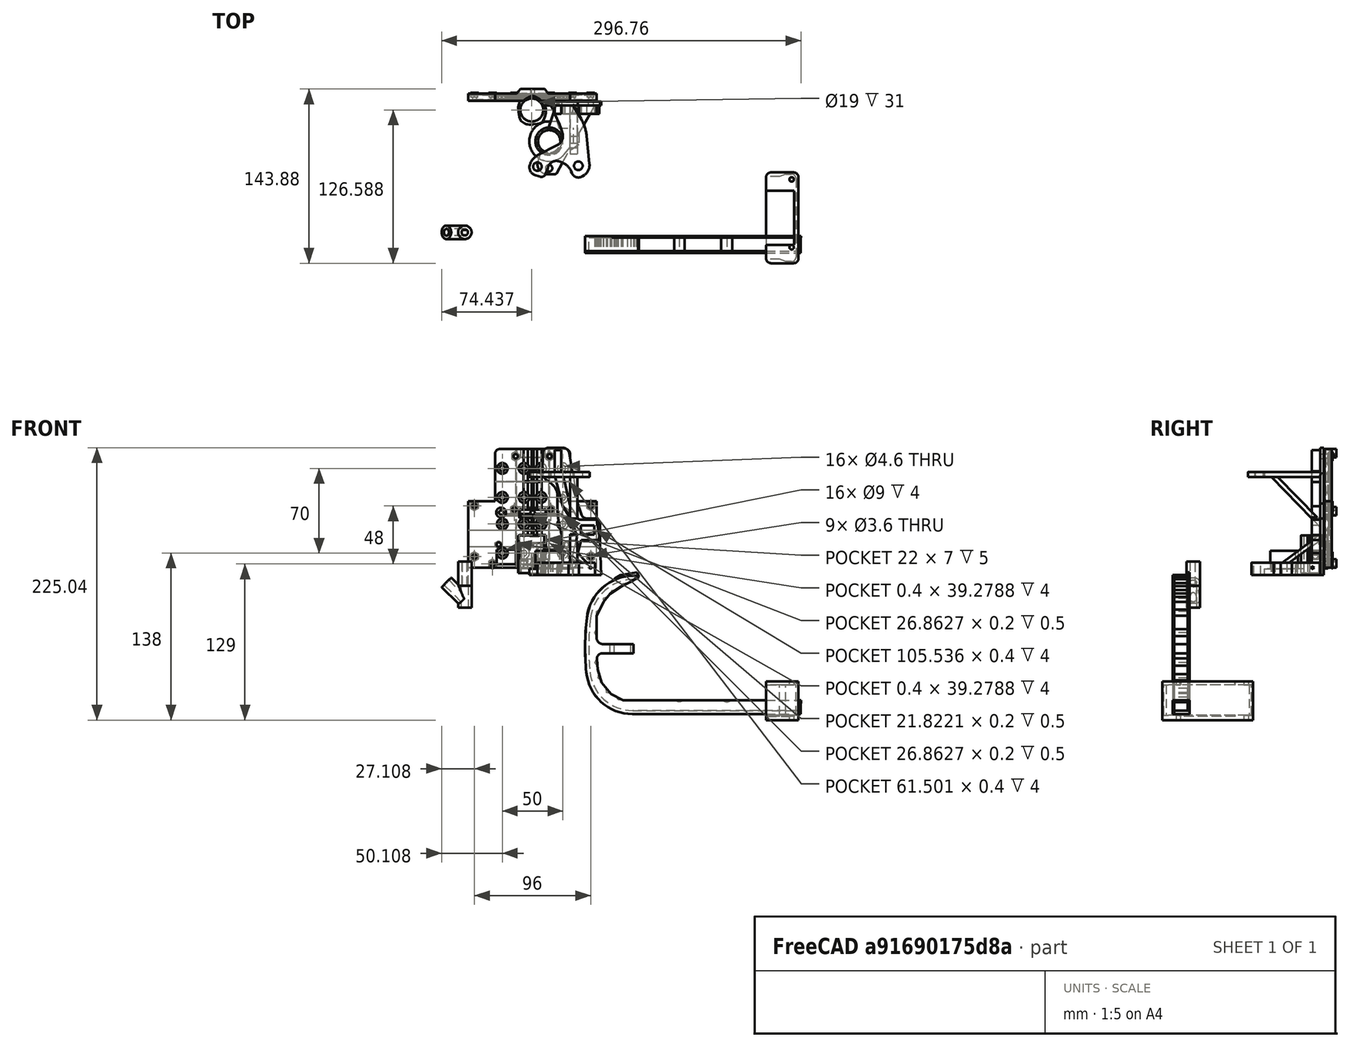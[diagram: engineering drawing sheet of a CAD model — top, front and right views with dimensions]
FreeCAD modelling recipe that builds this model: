
FCSTD DOCUMENT  (FreeCAD 0.18.4R)
Label: pick-and-place
License: All rights reserved
LicenseURL: http://en.wikipedia.org/wiki/All_rights_reserved
objects: Sketcher::SketchObject×44, PartDesign::Pad×22, PartDesign::Pocket×22, PartDesign::Body×8, PartDesign::LinearPattern×1, Mesh::Feature×1
note: 141 computed .brp shape members not serialized (recipe doc carries the construction recipe); baked Part::Feature solids carry a one-line shape summary decoded from their .brp

FEATURE [Sketcher::SketchObject] Sketch110
  AttachmentOffset = pos=(0,0,47) rot=(0,0,1;0rad)
  MapMode = 5
  Placement = pos=(0,-47,-1e-14) rot=(1,0,0;1.5708rad)
  sketch-geometry (4):
    g0: LineSegment StartX=-53 StartY=0 StartZ=0 EndX=53 EndY=0 EndZ=0
    g1: LineSegment StartX=53 StartY=0 StartZ=0 EndX=53 EndY=6 EndZ=0
    g2: LineSegment StartX=53 StartY=6 StartZ=0 EndX=-53 EndY=6 EndZ=0
    g3: LineSegment StartX=-53 StartY=6 StartZ=0 EndX=-53 EndY=0 EndZ=0
  constraints (11):
    c: Coincident(g0,g1)
    c: Coincident(g1,g2)
    c: Coincident(g2,g3)
    c: Coincident(g3,g0)
    c: Horizontal(g0)
    c: Vertical(g1)
    c: Vertical(g3)
    c: PointOnObject(g0,g-1)
    c: Symmetric(g2,g1,g-2)
    c: DistanceY(g1,g1) = 6
    c: DistanceX(g2,g2) = 106
FEATURE [Sketcher::SketchObject] Sketch020
  AttachmentOffset = pos=(-44,0,0) rot=(0,0,1;0rad)
  MapMode = 5
  Placement = pos=(-44,0,0) rot=(0,0,1;0rad)
  sketch-geometry (3):
    g0: Circle CenterX=18 CenterY=-1.5 CenterZ=0 NormalX=0 NormalY=0 NormalZ=1 AngleXU=0 Radius=1.75
    g1: Circle CenterX=44 CenterY=-1.5 CenterZ=0 NormalX=0 NormalY=0 NormalZ=1 AngleXU=0 Radius=1.75
    g2: Circle CenterX=70 CenterY=-1.5 CenterZ=0 NormalX=0 NormalY=0 NormalZ=1 AngleXU=0 Radius=1.75
  constraints (9):
    c: Equal(g1,g2)
    c: Diameter(g2) = 3.5
    c: DistanceX(g-1,g0) = 18
    c: DistanceX(g-1,g1) = 44
    c: DistanceX(g-1,g2) = 70
    c: DistanceY(g0,g-1) = 1.5
    c: Equal(g1,g0)
    c: DistanceY(g1,g0) = 0
    c: DistanceY(g2,g1) = 0
FEATURE [Sketcher::SketchObject] Sketch021
  AttachmentOffset = pos=(0,0,2) rot=(0,0,1;0rad)
  ExternalGeometry = -> [Sketch020]
  MapMode = 5
  Placement = pos=(0,0,2) rot=(0,0,1;0rad)
  sketch-geometry (3):
    g0: Circle CenterX=-26 CenterY=-1.5 CenterZ=0 NormalX=0 NormalY=0 NormalZ=1 AngleXU=0 Radius=3.1
    g1: Circle CenterX=0 CenterY=-1.5 CenterZ=0 NormalX=0 NormalY=0 NormalZ=1 AngleXU=0 Radius=3.1
    g2: Circle CenterX=26 CenterY=-1.5 CenterZ=0 NormalX=0 NormalY=0 NormalZ=1 AngleXU=0 Radius=3.1
  constraints (6):
    c: Coincident(g0,g-3)
    c: Coincident(g1,g-4)
    c: Coincident(g2,g-5)
    c: Equal(g0,g1)
    c: Equal(g1,g2)
    c: Diameter(g2) = 6.2
FEATURE [Sketcher::SketchObject] Sketch290  label="mount-holes"
  MapMode = 5
  sketch-geometry (23):
    g0: Circle CenterX=-25 CenterY=35 CenterZ=0 NormalX=0 NormalY=0 NormalZ=1 AngleXU=0 Radius=2.3
    g1: Circle CenterX=-7 CenterY=35 CenterZ=0 NormalX=0 NormalY=0 NormalZ=1 AngleXU=0 Radius=2.3
    g2: Circle CenterX=-25 CenterY=11 CenterZ=0 NormalX=0 NormalY=0 NormalZ=1 AngleXU=0 Radius=2.3
    g3: Circle CenterX=-7 CenterY=11 CenterZ=0 NormalX=0 NormalY=0 NormalZ=1 AngleXU=0 Radius=2.3
    g4: LineSegment [constr] StartX=-16 StartY=23 StartZ=0 EndX=16 EndY=23 EndZ=0
    g5: LineSegment [constr] StartX=-16 StartY=44 StartZ=0 EndX=-16 EndY=2 EndZ=0
    g6: LineSegment [constr] StartX=16 StartY=44 StartZ=0 EndX=16 EndY=2 EndZ=0
    g7: Circle CenterX=7 CenterY=35 CenterZ=0 NormalX=0 NormalY=0 NormalZ=1 AngleXU=0 Radius=2.3
    g8: Circle CenterX=25 CenterY=35 CenterZ=0 NormalX=0 NormalY=0 NormalZ=1 AngleXU=0 Radius=2.3
    g9: Circle CenterX=7 CenterY=11 CenterZ=0 NormalX=0 NormalY=0 NormalZ=1 AngleXU=0 Radius=2.3
    g10: Circle CenterX=25 CenterY=11 CenterZ=0 NormalX=0 NormalY=0 NormalZ=1 AngleXU=0 Radius=2.3
    g11: LineSegment [constr] StartX=-16 StartY=-23 StartZ=0 EndX=16 EndY=-23 EndZ=0
    g12: LineSegment [constr] StartX=1.74e-14 StartY=-2 StartZ=0 EndX=3.88e-14 EndY=-44 EndZ=0
    g13: Circle CenterX=-25 CenterY=-11 CenterZ=0 NormalX=0 NormalY=0 NormalZ=1 AngleXU=0 Radius=2.3
    g14: Circle CenterX=-7 CenterY=-11 CenterZ=0 NormalX=0 NormalY=0 NormalZ=1 AngleXU=0 Radius=2.3
    g15: Circle CenterX=-25 CenterY=-35 CenterZ=0 NormalX=0 NormalY=0 NormalZ=1 AngleXU=0 Radius=2.3
    g16: Circle CenterX=-7 CenterY=-35 CenterZ=0 NormalX=0 NormalY=0 NormalZ=1 AngleXU=0 Radius=2.3
    g17: LineSegment [constr] StartX=-16 StartY=-3.19826 StartZ=0 EndX=-16 EndY=-38.1346 EndZ=0
    g18: LineSegment [constr] StartX=16 StartY=-4.27965 StartZ=0 EndX=16 EndY=-37.7037 EndZ=0
    g19: Circle CenterX=7 CenterY=-11 CenterZ=0 NormalX=0 NormalY=0 NormalZ=1 AngleXU=0 Radius=2.3
    g20: Circle CenterX=25 CenterY=-11 CenterZ=0 NormalX=0 NormalY=0 NormalZ=1 AngleXU=0 Radius=2.3
    g21: Circle CenterX=7 CenterY=-35 CenterZ=0 NormalX=0 NormalY=0 NormalZ=1 AngleXU=0 Radius=2.3
    g22: Circle CenterX=25 CenterY=-35 CenterZ=0 NormalX=0 NormalY=0 NormalZ=1 AngleXU=0 Radius=2.3
  constraints (47):
    c: Symmetric(g0,g1,g5)
    c: Symmetric(g2,g3,g5)
    c: Symmetric(g0,g2,g4)
    c: DistanceX(g0,g1) = 18
    c: DistanceY(g3,g1) = 24
    c: Equal(g0,g1)
    c: Equal(g0,g2)
    c: Equal(g0,g3)
    c: Diameter(g0) = 4.6
    c: Equal(g1, g7-g10) x4
    c: Symmetric(g7,g9,g4)
    c: Symmetric(g7,g8,g6)
    c: Symmetric(g9,g10,g6)
    c: DistanceX(g7,g8) = 18
    c: Symmetric(g13,g15,g11)
    c: Equal(g2, g13-g16) x4
    c: Symmetric(g3,g9,g12)
    c: DistanceY(g11,g4) = 46
    c: Symmetric(g5,g5,g4)
    c: Symmetric(g6,g6,g4)
    c: Symmetric(g12,g12,g11)
    c: DistanceY(g5,g5) = 42
    c: DistanceY(g6,g6) = 42
    c: DistanceY(g12,g12) = 42
    c: Symmetric(g4,g4,g12)
    c: PointOnObject(g11,g5)
    c: PointOnObject(g11,g6)
    c: Symmetric(g4,g11,g-1)
    c: Symmetric(g1,g7,g-2)
    c: DistanceX(g13,g14) = 18
    c: DistanceY(g15,g13) = 24
    c: Symmetric(g13,g14,g17)
    c: Symmetric(g14,g16,g11)
    c: Symmetric(g15,g16,g17)
    c: DistanceX(g1,g7) = 14
    c: PointOnObject(g17,g5)
    c: Vertical(g18)
    c: PointOnObject(g18,g6)
    c: Equal(g9,g19)
    c: Equal(g19,g20)
    c: Equal(g20,g22)
    c: Equal(g22,g21)
    c: Symmetric(g19,g21,g11)
    c: Symmetric(g20,g22,g11)
    c: Symmetric(g19,g20,g18)
    c: DistanceX(g9,g19) = 0
    c: DistanceY(g19,g14) = 0
FEATURE [Sketcher::SketchObject] Sketch007
  AttachmentOffset = pos=(0,0,2) rot=(0,0,1;0rad)
  ExternalGeometry = -> [Sketch290,Sketch020]
  MapMode = 5
  Placement = pos=(0,0,2) rot=(0,0,1;0rad)
  sketch-geometry (19):
    g0: Circle CenterX=-25 CenterY=35 CenterZ=0 NormalX=0 NormalY=0 NormalZ=1 AngleXU=0 Radius=4.5
    g1: Circle CenterX=-7 CenterY=35 CenterZ=0 NormalX=0 NormalY=0 NormalZ=1 AngleXU=0 Radius=4.5
    g2: Circle CenterX=7 CenterY=35 CenterZ=0 NormalX=0 NormalY=0 NormalZ=1 AngleXU=0 Radius=4.5
    g3: Circle CenterX=25 CenterY=35 CenterZ=0 NormalX=0 NormalY=0 NormalZ=1 AngleXU=0 Radius=4.5
    g4: Circle CenterX=-25 CenterY=11 CenterZ=0 NormalX=0 NormalY=0 NormalZ=1 AngleXU=0 Radius=4.5
    g5: Circle CenterX=-7 CenterY=11 CenterZ=0 NormalX=0 NormalY=0 NormalZ=1 AngleXU=0 Radius=4.5
    g6: Circle CenterX=7 CenterY=11 CenterZ=0 NormalX=0 NormalY=0 NormalZ=1 AngleXU=0 Radius=4.5
    g7: Circle CenterX=25 CenterY=11 CenterZ=0 NormalX=0 NormalY=0 NormalZ=1 AngleXU=0 Radius=4.5
    g8: Circle CenterX=-25 CenterY=-11 CenterZ=0 NormalX=0 NormalY=0 NormalZ=1 AngleXU=0 Radius=4.5
    g9: Circle CenterX=-7 CenterY=-11 CenterZ=0 NormalX=0 NormalY=0 NormalZ=1 AngleXU=0 Radius=4.5
    g10: Circle CenterX=-25 CenterY=-35 CenterZ=0 NormalX=0 NormalY=0 NormalZ=1 AngleXU=0 Radius=4.5
    g11: Circle CenterX=-7 CenterY=-35 CenterZ=0 NormalX=0 NormalY=0 NormalZ=1 AngleXU=0 Radius=4.5
    g12: Circle CenterX=-26 CenterY=-1.5 CenterZ=0 NormalX=0 NormalY=0 NormalZ=1 AngleXU=0 Radius=4.1
    g13: Circle CenterX=0 CenterY=-1.5 CenterZ=0 NormalX=0 NormalY=0 NormalZ=1 AngleXU=0 Radius=4.1
    g14: Circle CenterX=26 CenterY=-1.5 CenterZ=0 NormalX=0 NormalY=0 NormalZ=1 AngleXU=0 Radius=4.1
    g15: Circle CenterX=7 CenterY=-11 CenterZ=0 NormalX=0 NormalY=0 NormalZ=1 AngleXU=0 Radius=4.5
    g16: Circle CenterX=25 CenterY=-11 CenterZ=0 NormalX=0 NormalY=0 NormalZ=1 AngleXU=0 Radius=4.5
    g17: Circle CenterX=7 CenterY=-35 CenterZ=0 NormalX=0 NormalY=0 NormalZ=1 AngleXU=0 Radius=4.5
    g18: Circle CenterX=25 CenterY=-35 CenterZ=0 NormalX=0 NormalY=0 NormalZ=1 AngleXU=0 Radius=4.5
FEATURE [Sketcher::SketchObject] Sketch001
  ExternalGeometry = -> [Sketch290]
  MapMode = 5
  sketch-geometry (8):
    g0: LineSegment StartX=-27 StartY=51 StartZ=0 EndX=27 EndY=51 EndZ=0
    g1: LineSegment StartX=31 StartY=47 StartZ=0 EndX=31 EndY=-43 EndZ=0
    g2: LineSegment StartX=27 StartY=-47 StartZ=0 EndX=-27 EndY=-47 EndZ=0
    g3: ArcOfCircle CenterX=-27 CenterY=47 CenterZ=0 NormalX=0 NormalY=0 NormalZ=1 AngleXU=0 Radius=4 StartAngle=1.5708 EndAngle=3.14159
    g4: ArcOfCircle CenterX=27 CenterY=47 CenterZ=0 NormalX=0 NormalY=0 NormalZ=1 AngleXU=0 Radius=4 StartAngle=6e-16 EndAngle=1.5708
    g5: ArcOfCircle CenterX=-27 CenterY=-43 CenterZ=0 NormalX=0 NormalY=0 NormalZ=1 AngleXU=0 Radius=4 StartAngle=3.14114 EndAngle=4.71239
    g6: ArcOfCircle CenterX=27 CenterY=-43 CenterZ=0 NormalX=0 NormalY=0 NormalZ=1 AngleXU=0 Radius=4 StartAngle=4.71239 EndAngle=6.28319
    g7: LineSegment StartX=-31 StartY=-42.9982 StartZ=0 EndX=-31 EndY=47 EndZ=0
  constraints (20):
    c: Horizontal(g2)
    c: Vertical(g1)
    c: Tangent(g0,g3) = 1.5708
    c: Tangent(g0,g4) = 1.5708
    c: Tangent(g1,g4) = 1.5708
    c: Tangent(g2,g5) = 1.5708
    c: Tangent(g2,g6) = 1.5708
    c: Tangent(g1,g6) = 1.5708
    c: Radius(g3) = 4
    c: Equal(g3,g4)
    c: Equal(g4,g6)
    c: Equal(g6,g5)
    c: Symmetric(g0,g0,g-2)
    c: DistanceY(g2,g-5) = 12
    c: DistanceY(g-3,g0) = 16
    c: Coincident(g7,g5)
    c: Vertical(g7)
    c: DistanceX(g3,g-3) = 6
    c: Coincident(g7,g3)
    c: Tangent(g3,g7)
FEATURE [PartDesign::Pad] Pad060
  Length = 6
  Length2 = 100
  Profile = -> Sketch001
  Type = 0
FEATURE [PartDesign::Pad] Pad016
  BaseFeature = -> Pad060
  Length = 55
  Length2 = 100
  Profile = -> Sketch110
  Reversed = true
  Type = 0
FEATURE [Sketcher::SketchObject] Sketch294
  MapMode = 5
  sketch-geometry (10):
    g0: Circle CenterX=-15 CenterY=1 CenterZ=0 NormalX=0 NormalY=0 NormalZ=1 AngleXU=0 Radius=1.8
    g1: Circle CenterX=-33 CenterY=-44 CenterZ=0 NormalX=0 NormalY=0 NormalZ=1 AngleXU=0 Radius=1.8
    g2: Circle CenterX=-48 CenterY=4 CenterZ=0 NormalX=0 NormalY=0 NormalZ=1 AngleXU=0 Radius=1.8
    g3: Circle CenterX=-48 CenterY=-38 CenterZ=0 NormalX=0 NormalY=0 NormalZ=1 AngleXU=0 Radius=1.8
    g4: Circle CenterX=15 CenterY=1 CenterZ=0 NormalX=0 NormalY=0 NormalZ=1 AngleXU=0 Radius=1.8
    g5: Circle CenterX=33 CenterY=-44 CenterZ=0 NormalX=0 NormalY=0 NormalZ=1 AngleXU=0 Radius=1.8
    g6: Circle CenterX=48 CenterY=-38 CenterZ=0 NormalX=0 NormalY=0 NormalZ=1 AngleXU=0 Radius=1.8
    g7: Circle CenterX=48 CenterY=4 CenterZ=0 NormalX=0 NormalY=0 NormalZ=1 AngleXU=0 Radius=1.8
    g8: Circle CenterX=-14 CenterY=45 CenterZ=0 NormalX=0 NormalY=0 NormalZ=1 AngleXU=0 Radius=1.8
    g9: Circle CenterX=14 CenterY=45 CenterZ=0 NormalX=0 NormalY=0 NormalZ=1 AngleXU=0 Radius=1.8
  constraints (25):
    c: Diameter(g1) = 3.6
    c: DistanceX(g1) = -33
    c: DistanceY(g1) = -44
    c: Equal(g1,g0)
    c: Equal(g0,g2)
    c: Equal(g2,g3)
    c: DistanceX(g3) = -48
    c: DistanceX(g2) = -48
    c: DistanceX(g0) = -15
    c: DistanceY(g0) = 1
    c: Equal(g0,g4)
    c: Equal(g4,g7)
    c: Equal(g7,g6)
    c: Equal(g6,g5)
    c: Symmetric(g1,g5,g-2)
    c: Symmetric(g6,g3,g-2)
    c: Symmetric(g2,g7,g-2)
    c: Symmetric(g0,g4,g-2)
    c: DistanceY(g-1,g2) = 4
    c: Equal(g8,g4)
    c: DistanceX(g8) = -14
    c: DistanceY(g8) = 45
    c: Symmetric(g8,g9,g-2)
    c: Equal(g8,g9)
    c: DistanceY(g3,g1) = -6
FEATURE [Sketcher::SketchObject] Sketch295
  AttachmentOffset = pos=(0,0,3) rot=(0,0,1;0rad)
  ExternalGeometry = -> [Sketch294]
  MapMode = 5
  Placement = pos=(0,0,3) rot=(0,0,1;0rad)
  sketch-geometry (70):
    g0: LineSegment StartX=-45.2 StartY=-36.3834 StartZ=0 EndX=-48 EndY=-34.7668 EndZ=0
    g1: LineSegment StartX=-48 StartY=-34.7668 StartZ=0 EndX=-50.8 EndY=-36.3834 EndZ=0
    g2: LineSegment StartX=-50.8 StartY=-36.3834 StartZ=0 EndX=-50.8 EndY=-39.6166 EndZ=0
    g3: LineSegment StartX=-50.8 StartY=-39.6166 StartZ=0 EndX=-48 EndY=-41.2332 EndZ=0
    g4: LineSegment StartX=-48 StartY=-41.2332 StartZ=0 EndX=-45.2 EndY=-39.6166 EndZ=0
    g5: LineSegment StartX=-45.2 StartY=-39.6166 StartZ=0 EndX=-45.2 EndY=-36.3834 EndZ=0
    g6: Circle [constr] CenterX=-48 CenterY=-38 CenterZ=0 NormalX=0 NormalY=0 NormalZ=1 AngleXU=0 Radius=3.23316
    g7: LineSegment StartX=-30.2 StartY=-42.3834 StartZ=0 EndX=-33 EndY=-40.7668 EndZ=0
    g8: LineSegment StartX=-33 StartY=-40.7668 StartZ=0 EndX=-35.8 EndY=-42.3834 EndZ=0
    g9: LineSegment StartX=-35.8 StartY=-42.3834 StartZ=0 EndX=-35.8 EndY=-45.6166 EndZ=0
    g10: LineSegment StartX=-35.8 StartY=-45.6166 StartZ=0 EndX=-33 EndY=-47.2332 EndZ=0
    g11: LineSegment StartX=-33 StartY=-47.2332 StartZ=0 EndX=-30.2 EndY=-45.6166 EndZ=0
    g12: LineSegment StartX=-30.2 StartY=-45.6166 StartZ=0 EndX=-30.2 EndY=-42.3834 EndZ=0
    g13: Circle [constr] CenterX=-33 CenterY=-44 CenterZ=0 NormalX=0 NormalY=0 NormalZ=1 AngleXU=0 Radius=3.23316
    g14: LineSegment StartX=-45.2 StartY=5.61658 StartZ=0 EndX=-48 EndY=7.23316 EndZ=0
    g15: LineSegment StartX=-48 StartY=7.23316 StartZ=0 EndX=-50.8 EndY=5.61658 EndZ=0
    g16: LineSegment StartX=-50.8 StartY=5.61658 StartZ=0 EndX=-50.8 EndY=2.38342 EndZ=0
    g17: LineSegment StartX=-50.8 StartY=2.38342 StartZ=0 EndX=-48 EndY=0.766838 EndZ=0
    g18: LineSegment StartX=-48 StartY=0.766838 StartZ=0 EndX=-45.2 EndY=2.38342 EndZ=0
    g19: LineSegment StartX=-45.2 StartY=2.38342 StartZ=0 EndX=-45.2 EndY=5.61658 EndZ=0
    g20: Circle [constr] CenterX=-48 CenterY=4 CenterZ=0 NormalX=0 NormalY=0 NormalZ=1 AngleXU=0 Radius=3.23316
    g21: LineSegment StartX=-12.2 StartY=2.61658 StartZ=0 EndX=-15 EndY=4.23316 EndZ=0
    g22: LineSegment StartX=-15 StartY=4.23316 StartZ=0 EndX=-17.8 EndY=2.61658 EndZ=0
    g23: LineSegment StartX=-17.8 StartY=2.61658 StartZ=0 EndX=-17.8 EndY=-0.616581 EndZ=0
    g24: LineSegment StartX=-17.8 StartY=-0.616581 StartZ=0 EndX=-15 EndY=-2.23316 EndZ=0
    g25: LineSegment StartX=-15 StartY=-2.23316 StartZ=0 EndX=-12.2 EndY=-0.616581 EndZ=0
    g26: LineSegment StartX=-12.2 StartY=-0.616581 StartZ=0 EndX=-12.2 EndY=2.61658 EndZ=0
    g27: Circle [constr] CenterX=-15 CenterY=1 CenterZ=0 NormalX=0 NormalY=0 NormalZ=1 AngleXU=0 Radius=3.23316
    g28: LineSegment StartX=-11.2 StartY=46.6166 StartZ=0 EndX=-14 EndY=48.2332 EndZ=0
    g29: LineSegment StartX=-14 StartY=48.2332 StartZ=0 EndX=-16.8 EndY=46.6166 EndZ=0
    g30: LineSegment StartX=-16.8 StartY=46.6166 StartZ=0 EndX=-16.8 EndY=43.3834 EndZ=0
    g31: LineSegment StartX=-16.8 StartY=43.3834 StartZ=0 EndX=-14 EndY=41.7668 EndZ=0
    g32: LineSegment StartX=-14 StartY=41.7668 StartZ=0 EndX=-11.2 EndY=43.3834 EndZ=0
    g33: LineSegment StartX=-11.2 StartY=43.3834 StartZ=0 EndX=-11.2 EndY=46.6166 EndZ=0
    g34: Circle [constr] CenterX=-14 CenterY=45 CenterZ=0 NormalX=0 NormalY=0 NormalZ=1 AngleXU=0 Radius=3.23316
    g35: LineSegment StartX=16.8 StartY=46.6166 StartZ=0 EndX=14 EndY=48.2332 EndZ=0
    g36: LineSegment StartX=14 StartY=48.2332 StartZ=0 EndX=11.2 EndY=46.6166 EndZ=0
    g37: LineSegment StartX=11.2 StartY=46.6166 StartZ=0 EndX=11.2 EndY=43.3834 EndZ=0
    g38: LineSegment StartX=11.2 StartY=43.3834 StartZ=0 EndX=14 EndY=41.7668 EndZ=0
    g39: LineSegment StartX=14 StartY=41.7668 StartZ=0 EndX=16.8 EndY=43.3834 EndZ=0
    g40: LineSegment StartX=16.8 StartY=43.3834 StartZ=0 EndX=16.8 EndY=46.6166 EndZ=0
    g41: Circle [constr] CenterX=14 CenterY=45 CenterZ=0 NormalX=0 NormalY=0 NormalZ=1 AngleXU=0 Radius=3.23316
    g42: LineSegment StartX=17.8 StartY=2.61658 StartZ=0 EndX=15 EndY=4.23316 EndZ=0
    g43: LineSegment StartX=15 StartY=4.23316 StartZ=0 EndX=12.2 EndY=2.61658 EndZ=0
    g44: LineSegment StartX=12.2 StartY=2.61658 StartZ=0 EndX=12.2 EndY=-0.616581 EndZ=0
    g45: LineSegment StartX=12.2 StartY=-0.616581 StartZ=0 EndX=15 EndY=-2.23316 EndZ=0
    g46: LineSegment StartX=15 StartY=-2.23316 StartZ=0 EndX=17.8 EndY=-0.616581 EndZ=0
    g47: LineSegment StartX=17.8 StartY=-0.616581 StartZ=0 EndX=17.8 EndY=2.61658 EndZ=0
    g48: Circle [constr] CenterX=15 CenterY=1 CenterZ=0 NormalX=0 NormalY=0 NormalZ=1 AngleXU=0 Radius=3.23316
    g49: LineSegment StartX=50.8 StartY=5.61658 StartZ=0 EndX=48 EndY=7.23316 EndZ=0
    g50: LineSegment StartX=48 StartY=7.23316 StartZ=0 EndX=45.2 EndY=5.61658 EndZ=0
    g51: LineSegment StartX=45.2 StartY=5.61658 StartZ=0 EndX=45.2 EndY=2.38342 EndZ=0
    g52: LineSegment StartX=45.2 StartY=2.38342 StartZ=0 EndX=48 EndY=0.766838 EndZ=0
    g53: LineSegment StartX=48 StartY=0.766838 StartZ=0 EndX=50.8 EndY=2.38342 EndZ=0
    g54: LineSegment StartX=50.8 StartY=2.38342 StartZ=0 EndX=50.8 EndY=5.61658 EndZ=0
    g55: Circle [constr] CenterX=48 CenterY=4 CenterZ=0 NormalX=0 NormalY=0 NormalZ=1 AngleXU=0 Radius=3.23316
    g56: LineSegment StartX=35.8 StartY=-42.3834 StartZ=0 EndX=33 EndY=-40.7668 EndZ=0
    g57: LineSegment StartX=33 StartY=-40.7668 StartZ=0 EndX=30.2 EndY=-42.3834 EndZ=0
    g58: LineSegment StartX=30.2 StartY=-42.3834 StartZ=0 EndX=30.2 EndY=-45.6166 EndZ=0
    g59: LineSegment StartX=30.2 StartY=-45.6166 StartZ=0 EndX=33 EndY=-47.2332 EndZ=0
    g60: LineSegment StartX=33 StartY=-47.2332 StartZ=0 EndX=35.8 EndY=-45.6166 EndZ=0
    g61: LineSegment StartX=35.8 StartY=-45.6166 StartZ=0 EndX=35.8 EndY=-42.3834 EndZ=0
    g62: Circle [constr] CenterX=33 CenterY=-44 CenterZ=0 NormalX=0 NormalY=0 NormalZ=1 AngleXU=0 Radius=3.23316
    g63: LineSegment StartX=50.8 StartY=-36.3834 StartZ=0 EndX=48 EndY=-34.7668 EndZ=0
    g64: LineSegment StartX=48 StartY=-34.7668 StartZ=0 EndX=45.2 EndY=-36.3834 EndZ=0
    g65: LineSegment StartX=45.2 StartY=-36.3834 StartZ=0 EndX=45.2 EndY=-39.6166 EndZ=0
    g66: LineSegment StartX=45.2 StartY=-39.6166 StartZ=0 EndX=48 EndY=-41.2332 EndZ=0
    g67: LineSegment StartX=48 StartY=-41.2332 StartZ=0 EndX=50.8 EndY=-39.6166 EndZ=0
    g68: LineSegment StartX=50.8 StartY=-39.6166 StartZ=0 EndX=50.8 EndY=-36.3834 EndZ=0
    g69: Circle [constr] CenterX=48 CenterY=-38 CenterZ=0 NormalX=0 NormalY=0 NormalZ=1 AngleXU=0 Radius=3.23316
  constraints (160):
    c: Coincident(g0,g1)
    c: Coincident(g1,g2)
    c: Coincident(g2,g3)
    c: Coincident(g3,g4)
    c: Coincident(g4,g5)
    c: Coincident(g5,g0)
    c: Equal(g0, g1-g5) x5
    c: PointOnObject(g0,g6)
    c: PointOnObject(g1,g6)
    c: PointOnObject(g2,g6)
    c: PointOnObject(g3,g6)
    c: PointOnObject(g4,g6)
    c: PointOnObject(g5,g6)
    c: Coincident(g6,g-6)
    c: Coincident(g7,g8)
    c: Coincident(g8,g9)
    c: Coincident(g9,g10)
    c: Coincident(g10,g11)
    c: Coincident(g11,g12)
    c: Coincident(g12,g7)
    c: Equal(g7, g8-g12) x5
    c: PointOnObject(g7,g13)
    c: PointOnObject(g8,g13)
    c: PointOnObject(g9,g13)
    c: PointOnObject(g10,g13)
    c: PointOnObject(g11,g13)
    c: PointOnObject(g12,g13)
    c: Coincident(g13,g-7)
    c: Coincident(g14,g15)
    c: Coincident(g15,g16)
    c: Coincident(g16,g17)
    c: Coincident(g17,g18)
    c: Coincident(g18,g19)
    c: Coincident(g19,g14)
    c: Equal(g14, g15-g19) x5
    c: PointOnObject(g14,g20)
    c: PointOnObject(g15,g20)
    c: PointOnObject(g16,g20)
    c: PointOnObject(g17,g20)
    c: PointOnObject(g18,g20)
    c: PointOnObject(g19,g20)
    c: Coincident(g20,g-3)
    c: Coincident(g21,g22)
    c: Coincident(g22,g23)
    c: Coincident(g23,g24)
    c: Coincident(g24,g25)
    c: Coincident(g25,g26)
    c: Coincident(g26,g21)
    c: Equal(g21, g22-g26) x5
    c: PointOnObject(g21,g27)
    c: PointOnObject(g22,g27)
    c: PointOnObject(g23,g27)
    c: PointOnObject(g24,g27)
    c: PointOnObject(g25,g27)
    c: PointOnObject(g26,g27)
    c: Coincident(g27,g-5)
    c: Coincident(g28,g29)
    c: Coincident(g29,g30)
    c: Coincident(g30,g31)
    c: Coincident(g31,g32)
    c: Coincident(g32,g33)
    c: Coincident(g33,g28)
    c: Equal(g28, g29-g33) x5
    c: PointOnObject(g28,g34)
    c: PointOnObject(g29,g34)
    c: PointOnObject(g30,g34)
    c: PointOnObject(g31,g34)
    c: PointOnObject(g32,g34)
    c: PointOnObject(g33,g34)
    c: Coincident(g34,g-11)
    c: Coincident(g35,g36)
    c: Coincident(g36,g37)
    c: Coincident(g37,g38)
    c: Coincident(g38,g39)
    c: Coincident(g39,g40)
    c: Coincident(g40,g35)
    c: Equal(g35, g36-g40) x5
    c: PointOnObject(g35,g41)
    c: PointOnObject(g36,g41)
    c: PointOnObject(g37,g41)
    c: PointOnObject(g38,g41)
    c: PointOnObject(g39,g41)
    c: PointOnObject(g40,g41)
    c: Coincident(g41,g-12)
    c: Coincident(g42,g43)
    c: Coincident(g43,g44)
    c: Coincident(g44,g45)
    c: Coincident(g45,g46)
    c: Coincident(g46,g47)
    c: Coincident(g47,g42)
    c: Equal(g42, g43-g47) x5
    c: PointOnObject(g42,g48)
    c: PointOnObject(g43,g48)
    c: PointOnObject(g44,g48)
    c: PointOnObject(g45,g48)
    c: PointOnObject(g46,g48)
    c: PointOnObject(g47,g48)
    c: Coincident(g48,g-4)
    c: Coincident(g49,g50)
    c: Coincident(g50,g51)
    c: Coincident(g51,g52)
    c: Coincident(g52,g53)
    c: Coincident(g53,g54)
    c: Coincident(g54,g49)
    c: Equal(g49, g50-g54) x5
    c: PointOnObject(g49,g55)
    c: PointOnObject(g50,g55)
    c: PointOnObject(g51,g55)
    c: PointOnObject(g52,g55)
    c: PointOnObject(g53,g55)
    c: PointOnObject(g54,g55)
    c: Coincident(g55,g-10)
    c: Coincident(g56,g57)
    c: Coincident(g57,g58)
    c: Coincident(g58,g59)
    c: Coincident(g59,g60)
    c: Coincident(g60,g61)
    c: Coincident(g61,g56)
    c: Equal(g56, g57-g61) x5
    c: PointOnObject(g56,g62)
    c: PointOnObject(g57,g62)
    c: PointOnObject(g58,g62)
    c: PointOnObject(g59,g62)
    c: PointOnObject(g60,g62)
    c: PointOnObject(g61,g62)
    c: Coincident(g62,g-8)
    c: Coincident(g63,g64)
    c: Coincident(g64,g65)
    c: Coincident(g65,g66)
    c: Coincident(g66,g67)
    c: Coincident(g67,g68)
    c: Coincident(g68,g63)
    c: Equal(g63, g64-g68) x5
    c: PointOnObject(g63,g69)
    c: PointOnObject(g64,g69)
    c: PointOnObject(g65,g69)
    c: PointOnObject(g66,g69)
    c: PointOnObject(g67,g69)
    c: PointOnObject(g68,g69)
    c: Coincident(g69,g-9)
    c: Vertical(g5)
    c: Vertical(g12)
    c: Vertical(g61)
    c: Vertical(g68)
    c: Vertical(g54)
    c: Vertical(g47)
    c: Vertical(g40)
    c: Vertical(g33)
    c: Vertical(g26)
    c: Vertical(g19)
    c: DistanceX(g29,g28) = 5.6
    c: Equal(g33,g40)
    c: Equal(g40,g19)
    c: Equal(g19,g26)
    c: Equal(g26,g47)
    c: Equal(g47,g54)
    c: Equal(g68,g54)
    c: Equal(g68,g61)
    c: Equal(g61,g12)
    c: Equal(g5,g12)
FEATURE [Sketcher::SketchObject] Sketch299
  AttachmentOffset = pos=(0,0,5) rot=(0,0,1;0rad)
  MapMode = 5
  Placement = pos=(0,0,5) rot=(0,0,1;0rad)
  sketch-geometry (28):
    g0: LineSegment StartX=-30.7505 StartY=24.2507 StartZ=0 EndX=30.7505 EndY=24.2507 EndZ=0
    g1: LineSegment StartX=30.7505 StartY=24.2507 StartZ=0 EndX=30.7505 EndY=23.8507 EndZ=0
    g2: LineSegment StartX=30.7505 StartY=23.8507 StartZ=0 EndX=-30.7505 EndY=23.8507 EndZ=0
    g3: LineSegment StartX=-30.7505 StartY=23.8507 StartZ=0 EndX=-30.7505 EndY=24.2507 EndZ=0
    g4: LineSegment StartX=-52.7681 StartY=-15.8802 StartZ=0 EndX=52.7681 EndY=-15.8802 EndZ=0
    g5: LineSegment StartX=52.7681 StartY=-15.8802 StartZ=0 EndX=52.7681 EndY=-16.2802 EndZ=0
    g6: LineSegment StartX=52.7681 StartY=-16.2802 StartZ=0 EndX=-52.7681 EndY=-16.2802 EndZ=0
    g7: LineSegment StartX=-52.7681 StartY=-16.2802 StartZ=0 EndX=-52.7681 EndY=-15.8802 EndZ=0
    g8: LineSegment StartX=-52.749 StartY=-29.5495 StartZ=0 EndX=52.749 EndY=-29.5495 EndZ=0
    g9: LineSegment StartX=52.749 StartY=-29.5495 StartZ=0 EndX=52.749 EndY=-29.9495 EndZ=0
    g10: LineSegment StartX=52.749 StartY=-29.9495 StartZ=0 EndX=-52.749 EndY=-29.9495 EndZ=0
    g11: LineSegment StartX=-52.749 StartY=-29.9495 StartZ=0 EndX=-52.749 EndY=-29.5495 EndZ=0
    g12: LineSegment StartX=-13.8862 StartY=50.9099 StartZ=0 EndX=-13.4862 EndY=50.9099 EndZ=0
    g13: LineSegment StartX=-13.4862 StartY=50.9099 StartZ=0 EndX=-13.4862 EndY=0.587471 EndZ=0
    g14: LineSegment StartX=-13.4862 StartY=0.587471 StartZ=0 EndX=-13.8862 EndY=0.587471 EndZ=0
    g15: LineSegment StartX=-13.8862 StartY=0.587471 StartZ=0 EndX=-13.8862 EndY=50.9099 EndZ=0
    g16: LineSegment StartX=13.4862 StartY=50.9099 StartZ=0 EndX=13.8862 EndY=50.9099 EndZ=0
    g17: LineSegment StartX=13.8862 StartY=50.9099 StartZ=0 EndX=13.8862 EndY=0.587471 EndZ=0
    g18: LineSegment StartX=13.8862 StartY=0.587471 StartZ=0 EndX=13.4862 EndY=0.587471 EndZ=0
    g19: LineSegment StartX=13.4862 StartY=0.587471 StartZ=0 EndX=13.4862 EndY=50.9099 EndZ=0
    g20: LineSegment StartX=13.4862 StartY=-7.08749 StartZ=0 EndX=13.8862 EndY=-7.08749 EndZ=0
    g21: LineSegment StartX=13.8862 StartY=-7.08749 StartZ=0 EndX=13.8862 EndY=-46.3663 EndZ=0
    g22: LineSegment StartX=13.8862 StartY=-46.3663 StartZ=0 EndX=13.4862 EndY=-46.3663 EndZ=0
    g23: LineSegment StartX=13.4862 StartY=-46.3663 StartZ=0 EndX=13.4862 EndY=-7.08749 EndZ=0
    g24: LineSegment StartX=-13.8862 StartY=-7.08749 StartZ=0 EndX=-13.4862 EndY=-7.08749 EndZ=0
    g25: LineSegment StartX=-13.4862 StartY=-7.08749 StartZ=0 EndX=-13.4862 EndY=-46.3663 EndZ=0
    g26: LineSegment StartX=-13.4862 StartY=-46.3663 StartZ=0 EndX=-13.8862 EndY=-46.3663 EndZ=0
    g27: LineSegment StartX=-13.8862 StartY=-46.3663 StartZ=0 EndX=-13.8862 EndY=-7.08749 EndZ=0
  constraints (66):
    c: Coincident(g0,g1)
    c: Coincident(g1,g2)
    c: Coincident(g2,g3)
    c: Coincident(g3,g0)
    c: Horizontal(g2)
    c: Vertical(g1)
    c: Vertical(g3)
    c: Coincident(g4,g5)
    c: Coincident(g5,g6)
    c: Coincident(g6,g7)
    c: Coincident(g7,g4)
    c: Horizontal(g6)
    c: Vertical(g5)
    c: Vertical(g7)
    c: Coincident(g8,g9)
    c: Coincident(g9,g10)
    c: Coincident(g10,g11)
    c: Coincident(g11,g8)
    c: Horizontal(g10)
    c: Vertical(g9)
    c: Vertical(g11)
    c: Coincident(g12,g13)
    c: Coincident(g13,g14)
    c: Coincident(g14,g15)
    c: Coincident(g15,g12)
    c: Horizontal(g12)
    c: Horizontal(g14)
    c: Vertical(g13)
    c: Vertical(g15)
    c: Coincident(g16,g17)
    c: Coincident(g17,g18)
    c: Coincident(g18,g19)
    c: Coincident(g19,g16)
    c: Horizontal(g16)
    c: Horizontal(g18)
    c: Vertical(g17)
    c: DistanceY(g5,g5) = 0.4
    c: Equal(g5,g9)
    c: Equal(g9,g16)
    c: Equal(g16,g12)
    c: Symmetric(g12,g16,g-2)
    c: Equal(g16,g1)
    c: Symmetric(g0,g0,g-2)
    c: Symmetric(g4,g4,g-2)
    c: Symmetric(g8,g8,g-2)
    c: Symmetric(g13,g18,g-2)
    c: Coincident(g20,g21)
    c: Coincident(g21,g22)
    c: Coincident(g22,g23)
    c: Coincident(g23,g20)
    c: Horizontal(g20)
    c: Horizontal(g22)
    c: Vertical(g21)
    c: Vertical(g23)
    c: Coincident(g24,g25)
    c: Coincident(g25,g26)
    c: Coincident(g26,g27)
    c: Coincident(g27,g24)
    c: Horizontal(g24)
    c: Horizontal(g26)
    c: Vertical(g27)
    c: PointOnObject(g24,g15)
    c: PointOnObject(g24,g13)
    c: PointOnObject(g20,g17)
    c: Symmetric(g24,g20,g-2)
    c: Symmetric(g25,g22,g-2)
FEATURE [Sketcher::SketchObject] Sketch300
  AttachmentOffset = pos=(0,0,0.5) rot=(0,0,1;0rad)
  MapMode = 5
  Placement = pos=(0,0,0.5) rot=(0,0,1;0rad)
  sketch-geometry (16):
    g0: LineSegment StartX=-23.8387 StartY=-2.6808 StartZ=0 EndX=-2.0166 EndY=-2.6808 EndZ=0
    g1: LineSegment StartX=-2.0166 StartY=-2.6808 StartZ=0 EndX=-2.0166 EndY=-2.4808 EndZ=0
    g2: LineSegment StartX=-2.0166 StartY=-2.4808 StartZ=0 EndX=-23.8387 EndY=-2.4808 EndZ=0
    g3: LineSegment StartX=-23.8387 StartY=-2.4808 StartZ=0 EndX=-23.8387 EndY=-2.6808 EndZ=0
    g4: LineSegment StartX=-27.5679 StartY=-4.24296 StartZ=0 EndX=-0.705224 EndY=-4.24296 EndZ=0
    g5: LineSegment StartX=-0.705224 StartY=-4.24296 StartZ=0 EndX=-0.705224 EndY=-4.44296 EndZ=0
    g6: LineSegment StartX=-0.705224 StartY=-4.44296 StartZ=0 EndX=-27.5679 EndY=-4.44296 EndZ=0
    g7: LineSegment StartX=-27.5679 StartY=-4.44296 StartZ=0 EndX=-27.5679 EndY=-4.24296 EndZ=0
    g8: LineSegment StartX=2.0166 StartY=-2.4808 StartZ=0 EndX=23.8387 EndY=-2.4808 EndZ=0
    g9: LineSegment StartX=23.8387 StartY=-2.4808 StartZ=0 EndX=23.8387 EndY=-2.6808 EndZ=0
    g10: LineSegment StartX=23.8387 StartY=-2.6808 StartZ=0 EndX=2.0166 EndY=-2.6808 EndZ=0
    g11: LineSegment StartX=2.0166 StartY=-2.6808 StartZ=0 EndX=2.0166 EndY=-2.4808 EndZ=0
    g12: LineSegment StartX=0.705224 StartY=-4.24296 StartZ=0 EndX=27.5679 EndY=-4.24296 EndZ=0
    g13: LineSegment StartX=27.5679 StartY=-4.24296 StartZ=0 EndX=27.5679 EndY=-4.44296 EndZ=0
    g14: LineSegment StartX=27.5679 StartY=-4.44296 StartZ=0 EndX=0.705224 EndY=-4.44296 EndZ=0
    g15: LineSegment StartX=0.705224 StartY=-4.44296 StartZ=0 EndX=0.705224 EndY=-4.24296 EndZ=0
  constraints (36):
    c: Coincident(g0,g1)
    c: Coincident(g1,g2)
    c: Coincident(g2,g3)
    c: Coincident(g3,g0)
    c: Horizontal(g0)
    c: Horizontal(g2)
    c: Vertical(g1)
    c: Vertical(g3)
    c: Coincident(g4,g5)
    c: Coincident(g5,g6)
    c: Coincident(g6,g7)
    c: Coincident(g7,g4)
    c: Horizontal(g4)
    c: Horizontal(g6)
    c: Vertical(g5)
    c: Vertical(g7)
    c: Coincident(g8,g9)
    c: Coincident(g9,g10)
    c: Coincident(g10,g11)
    c: Coincident(g11,g8)
    c: Horizontal(g10)
    c: Vertical(g9)
    c: Coincident(g12,g13)
    c: Coincident(g13,g14)
    c: Coincident(g14,g15)
    c: Coincident(g15,g12)
    c: Horizontal(g14)
    c: Vertical(g13)
    c: DistanceY(g1,g1) = 0.2
    c: DistanceY(g5,g5) = 0.2
    c: Symmetric(g1,g8,g-2)
    c: Symmetric(g0,g10,g-2)
    c: Symmetric(g4,g12,g-2)
    c: Symmetric(g5,g14,g-2)
    c: Symmetric(g2,g8,g-2)
    c: Symmetric(g4,g12,g-2)
FEATURE [Sketcher::SketchObject] Sketch301
  AttachmentOffset = pos=(0,0,2.5) rot=(0,0,1;0rad)
  MapMode = 5
  Placement = pos=(0,0,2.5) rot=(0,0,1;0rad)
  sketch-geometry (16):
    g0: LineSegment StartX=-22.0391 StartY=-2.91528 StartZ=0 EndX=-4.05126 EndY=-2.91528 EndZ=0
    g1: LineSegment StartX=-4.05126 StartY=-2.91528 StartZ=0 EndX=-4.05126 EndY=-2.71528 EndZ=0
    g2: LineSegment StartX=-4.05126 StartY=-2.71528 StartZ=0 EndX=-22.0391 EndY=-2.71528 EndZ=0
    g3: LineSegment StartX=-22.0391 StartY=-2.71528 StartZ=0 EndX=-22.0391 EndY=-2.91528 EndZ=0
    g4: LineSegment StartX=-22.7206 StartY=-3.98038 StartZ=0 EndX=-3.36995 EndY=-3.98038 EndZ=0
    g5: LineSegment StartX=-3.36995 StartY=-3.98038 StartZ=0 EndX=-3.36995 EndY=-4.18038 EndZ=0
    g6: LineSegment StartX=-3.36995 StartY=-4.18038 StartZ=0 EndX=-22.7206 EndY=-4.18038 EndZ=0
    g7: LineSegment StartX=-22.7206 StartY=-4.18038 StartZ=0 EndX=-22.7206 EndY=-3.98038 EndZ=0
    g8: LineSegment StartX=4.05126 StartY=-2.71528 StartZ=0 EndX=22.0391 EndY=-2.71528 EndZ=0
    g9: LineSegment StartX=22.0391 StartY=-2.71528 StartZ=0 EndX=22.0391 EndY=-2.91528 EndZ=0
    g10: LineSegment StartX=22.0391 StartY=-2.91528 StartZ=0 EndX=4.05126 EndY=-2.91528 EndZ=0
    g11: LineSegment StartX=4.05126 StartY=-2.91528 StartZ=0 EndX=4.05126 EndY=-2.71528 EndZ=0
    g12: LineSegment StartX=3.36995 StartY=-3.98038 StartZ=0 EndX=22.7206 EndY=-3.98038 EndZ=0
    g13: LineSegment StartX=22.7206 StartY=-3.98038 StartZ=0 EndX=22.7206 EndY=-4.18038 EndZ=0
    g14: LineSegment StartX=22.7206 StartY=-4.18038 StartZ=0 EndX=3.36995 EndY=-4.18038 EndZ=0
    g15: LineSegment StartX=3.36995 StartY=-4.18038 StartZ=0 EndX=3.36995 EndY=-3.98038 EndZ=0
  constraints (36):
    c: Coincident(g0,g1)
    c: Coincident(g1,g2)
    c: Coincident(g2,g3)
    c: Coincident(g3,g0)
    c: Horizontal(g0)
    c: Horizontal(g2)
    c: Vertical(g1)
    c: Vertical(g3)
    c: Coincident(g4,g5)
    c: Coincident(g5,g6)
    c: Coincident(g6,g7)
    c: Coincident(g7,g4)
    c: Horizontal(g4)
    c: Horizontal(g6)
    c: Vertical(g5)
    c: Vertical(g7)
    c: Coincident(g8,g9)
    c: Coincident(g9,g10)
    c: Coincident(g10,g11)
    c: Coincident(g11,g8)
    c: Horizontal(g10)
    c: Vertical(g9)
    c: Coincident(g12,g13)
    c: Coincident(g13,g14)
    c: Coincident(g14,g15)
    c: Coincident(g15,g12)
    c: Horizontal(g14)
    c: Vertical(g13)
    c: DistanceY(g1,g1) = 0.2
    c: DistanceY(g5,g5) = 0.2
    c: Symmetric(g1,g8,g-2)
    c: Symmetric(g0,g10,g-2)
    c: Symmetric(g4,g12,g-2)
    c: Symmetric(g5,g14,g-2)
    c: Symmetric(g2,g8,g-2)
    c: Symmetric(g4,g12,g-2)
FEATURE [Sketcher::SketchObject] Sketch396
  MapMode = 5
  Placement = pos=(0,0,0) rot=(1,0,0;1.5708rad)
  Support = -> [XZ_Plane027]
  sketch-geometry (4):
    g0: ArcOfCircle CenterX=0 CenterY=12 CenterZ=0 NormalX=0 NormalY=0 NormalZ=1 AngleXU=0 Radius=9.5 StartAngle=5.12156 EndAngle=10.5864
    g1: ArcOfCircle CenterX=0 CenterY=8.45957 CenterZ=0 NormalX=0 NormalY=0 NormalZ=1 AngleXU=0 Radius=6.40855 StartAngle=4.08161 EndAngle=4.57853
    g2: ArcOfCircle CenterX=0 CenterY=3.37716 CenterZ=0 NormalX=0 NormalY=0 NormalZ=1 AngleXU=0 Radius=1.53016 StartAngle=4.11928 EndAngle=5.3055
    g3: ArcOfCircle CenterX=0 CenterY=8.45957 CenterZ=0 NormalX=0 NormalY=0 NormalZ=1 AngleXU=0 Radius=6.40855 StartAngle=4.84625 EndAngle=5.34317
  constraints (11):
    c: PointOnObject(g0,g-2)
    c: Diameter(g0) = 19
    c: DistanceY(g-1,g0) = 12
    c: Coincident(g0,g3)
    c: PointOnObject(g1,g-2)
    c: Coincident(g0,g1)
    c: PointOnObject(g2,g-2)
    c: Equal(g1,g3)
    c: Coincident(g1,g2)
    c: Coincident(g3,g2)
    c: Coincident(g1,g3)
FEATURE [Sketcher::SketchObject] Sketch397
  MapMode = 5
  Support = -> [XY_Plane027]
  sketch-geometry (1):
    g0: Circle CenterX=0 CenterY=-44 CenterZ=0 NormalX=0 NormalY=0 NormalZ=1 AngleXU=0 Radius=1.5
  constraints (3):
    c: Diameter(g0) = 3
    c: DistanceY(g0,g-1) = 44
    c: PointOnObject(g0,g-2)
FEATURE [Sketcher::SketchObject] Sketch398
  AttachmentOffset = pos=(0,0,3) rot=(0,0,1;0rad)
  ExternalGeometry = -> [Sketch397]
  MapMode = 5
  Placement = pos=(0,0,3) rot=(0,0,1;0rad)
  Support = -> [XY_Plane027]
  sketch-geometry (1):
    g0: Circle CenterX=0 CenterY=-43.9886 CenterZ=0 NormalX=0 NormalY=0 NormalZ=1 AngleXU=0 Radius=1.8
  constraints (2):
    c: PointOnObject(g0,g-2)
    c: Diameter(g0) = 3.6
FEATURE [Sketcher::SketchObject] Sketch592
  AttachmentOffset = pos=(0,0,-3) rot=(0,0,1;0rad)
  MapMode = 5
  Placement = pos=(0,3,7e-16) rot=(1,0,0;1.5708rad)
  Support = -> [XZ_Plane027]
  sketch-geometry (4):
    g0: LineSegment StartX=-13 StartY=-4e-16 StartZ=0 EndX=13 EndY=0 EndZ=0
    g1: LineSegment StartX=13 StartY=0 StartZ=0 EndX=10 EndY=-3.8 EndZ=0
    g2: LineSegment StartX=10 StartY=-3.8 StartZ=0 EndX=-10 EndY=-3.8 EndZ=0
    g3: LineSegment StartX=-10 StartY=-3.8 StartZ=0 EndX=-13 EndY=-4e-16 EndZ=0
  constraints (10):
    c: PointOnObject(g0,g-1)
    c: Coincident(g0,g1)
    c: Coincident(g1,g2)
    c: Coincident(g2,g3)
    c: Coincident(g3,g0)
    c: Symmetric(g0,g0,g-2)
    c: Symmetric(g2,g1,g-2)
    c: DistanceX(g0,g0) = 26
    c: DistanceX(g2,g2) = 20
    c: DistanceY(g1,g-1) = 3.8
FEATURE [PartDesign::Pad] Pad226
  BaseFeature = -> Pad016
  Length = 7
  Length2 = 100
  Profile = -> Sketch592
  Type = 0
FEATURE [Sketcher::SketchObject] Sketch593
  AttachmentOffset = pos=(0,0,40) rot=(0,0,1;0rad)
  MapMode = 5
  Placement = pos=(0,-40,-8.9e-15) rot=(1,0,0;1.5708rad)
  Support = -> [XZ_Plane027]
  sketch-geometry (4):
    g0: LineSegment StartX=-13 StartY=-4e-16 StartZ=0 EndX=13 EndY=0 EndZ=0
    g1: LineSegment StartX=13 StartY=0 StartZ=0 EndX=10 EndY=-3.8 EndZ=0
    g2: LineSegment StartX=10 StartY=-3.8 StartZ=0 EndX=-10 EndY=-3.8 EndZ=0
    g3: LineSegment StartX=-10 StartY=-3.8 StartZ=0 EndX=-13 EndY=-4e-16 EndZ=0
  constraints (10):
    c: PointOnObject(g0,g-1)
    c: Coincident(g0,g1)
    c: Coincident(g1,g2)
    c: Coincident(g2,g3)
    c: Coincident(g3,g0)
    c: Symmetric(g0,g0,g-2)
    c: Symmetric(g2,g1,g-2)
    c: DistanceX(g0,g0) = 26
    c: DistanceX(g2,g2) = 20
    c: DistanceY(g1,g-1) = 3.8
FEATURE [PartDesign::Pad] Pad227
  BaseFeature = -> Pad226
  Length = 7
  Length2 = 100
  Profile = -> Sketch593
  Type = 0
FEATURE [Sketcher::SketchObject] Sketch594
  AttachmentOffset = pos=(0,0,-51) rot=(0,0,1;0rad)
  MapMode = 5
  Placement = pos=(0,51,1.13e-14) rot=(1,0,0;1.5708rad)
  Support = -> [XZ_Plane027]
  sketch-geometry (4):
    g0: LineSegment StartX=-13 StartY=-4e-16 StartZ=0 EndX=13 EndY=0 EndZ=0
    g1: LineSegment StartX=13 StartY=0 StartZ=0 EndX=10 EndY=-3.8 EndZ=0
    g2: LineSegment StartX=10 StartY=-3.8 StartZ=0 EndX=-10 EndY=-3.8 EndZ=0
    g3: LineSegment StartX=-10 StartY=-3.8 StartZ=0 EndX=-13 EndY=-4e-16 EndZ=0
  constraints (10):
    c: PointOnObject(g0,g-1)
    c: Coincident(g0,g1)
    c: Coincident(g1,g2)
    c: Coincident(g2,g3)
    c: Coincident(g3,g0)
    c: Symmetric(g0,g0,g-2)
    c: Symmetric(g2,g1,g-2)
    c: DistanceX(g0,g0) = 26
    c: DistanceX(g2,g2) = 20
    c: DistanceY(g1,g-1) = 3.8
FEATURE [PartDesign::Pad] Pad228
  BaseFeature = -> Pad227
  Length = 7
  Length2 = 100
  Profile = -> Sketch594
  Type = 0
FEATURE [PartDesign::Pocket] Pocket008
  BaseFeature = -> Pad228
  Length = 5
  Length2 = 100
  Midplane = true
  Profile = -> Sketch020
  Reversed = true
  Type = 1
FEATURE [PartDesign::Pocket] Pocket009
  BaseFeature = -> Pocket008
  Length = 5
  Length2 = 100
  Profile = -> Sketch021
  Reversed = true
  Type = 0
FEATURE [PartDesign::Pocket] Pocket005
  BaseFeature = -> Pocket009
  Length = 5
  Length2 = 100
  Profile = -> Sketch290
  Reversed = true
  Type = 1
FEATURE [PartDesign::Pocket] Pocket006
  BaseFeature = -> Pocket005
  Length = 30
  Length2 = 100
  Profile = -> Sketch007
  Reversed = true
  Type = 0
FEATURE [PartDesign::Pocket] Pocket028
  BaseFeature = -> Pocket006
  Length = 5
  Length2 = 100
  Midplane = true
  Profile = -> Sketch294
  Type = 1
FEATURE [PartDesign::Pocket] Pocket029
  BaseFeature = -> Pocket028
  Length = 5
  Length2 = 100
  Profile = -> Sketch295
  Type = 1
FEATURE [PartDesign::Pocket] Pocket032
  BaseFeature = -> Pocket029
  Length = 4
  Length2 = 100
  Profile = -> Sketch299
  Type = 0
FEATURE [PartDesign::Pocket] Pocket033
  BaseFeature = -> Pocket032
  Length = 1
  Length2 = 100
  Profile = -> Sketch300
  Reversed = true
  Type = 0
FEATURE [PartDesign::Pocket] Pocket034
  BaseFeature = -> Pocket033
  Length = 3
  Length2 = 100
  Profile = -> Sketch301
  Reversed = true
  Type = 0
FEATURE [PartDesign::Pocket] Pocket101
  BaseFeature = -> Pocket034
  Length = 5
  Length2 = 100
  Midplane = true
  Profile = -> Sketch396
  Type = 1
FEATURE [PartDesign::Pocket] Pocket102
  BaseFeature = -> Pocket101
  Length = 5
  Length2 = 100
  Profile = -> Sketch397
  Reversed = true
  Type = 1
FEATURE [PartDesign::Pocket] Pocket103
  BaseFeature = -> Pocket102
  Length = 5
  Length2 = 100
  Profile = -> Sketch398
  Type = 1
FEATURE [Sketcher::SketchObject] Sketch787
  AttachmentOffset = pos=(0,0,-1) rot=(0,0,1;0rad)
  ExternalGeometry = -> [Sketch396]
  MapMode = 5
  Placement = pos=(0,1,2e-16) rot=(1,0,0;1.5708rad)
  Support = -> [XZ_Plane027]
  sketch-geometry (4):
    g0: LineSegment StartX=-11 StartY=12 StartZ=0 EndX=11 EndY=12 EndZ=0
    g1: LineSegment StartX=11 StartY=12 StartZ=0 EndX=11 EndY=1 EndZ=0
    g2: LineSegment StartX=11 StartY=1 StartZ=0 EndX=-11 EndY=1 EndZ=0
    g3: LineSegment StartX=-11 StartY=1 StartZ=0 EndX=-11 EndY=12 EndZ=0
  constraints (11):
    c: Coincident(g0,g1)
    c: Coincident(g1,g2)
    c: Coincident(g2,g3)
    c: Coincident(g3,g0)
    c: Horizontal(g2)
    c: Vertical(g1)
    c: Vertical(g3)
    c: DistanceX(g0,g0) = 22
    c: PointOnObject(g-3,g0)
    c: DistanceY(g-1,g1) = 1
    c: Symmetric(g0,g0,g-2)
FEATURE [PartDesign::Pocket] Pocket208
  BaseFeature = -> Pocket103
  Length = 7
  Length2 = 100
  Profile = -> Sketch787
  Reversed = true
  Type = 0
FEATURE [Sketcher::SketchObject] Sketch799
  ExternalGeometry = -> [Sketch294]
  MapMode = 5
  Support = -> [XY_Plane027]
  sketch-geometry (140):
    g0: LineSegment StartX=-45.2 StartY=2.38342 StartZ=0 EndX=-45.2 EndY=5.61658 EndZ=0
    g1: LineSegment StartX=-45.2 StartY=5.61658 StartZ=0 EndX=-48 EndY=7.23316 EndZ=0
    g2: LineSegment StartX=-48 StartY=7.23316 StartZ=0 EndX=-50.8 EndY=5.61658 EndZ=0
    g3: LineSegment StartX=-50.8 StartY=5.61658 StartZ=0 EndX=-50.8 EndY=2.38342 EndZ=0
    g4: LineSegment StartX=-50.8 StartY=2.38342 StartZ=0 EndX=-48 EndY=0.766838 EndZ=0
    g5: LineSegment StartX=-48 StartY=0.766838 StartZ=0 EndX=-45.2 EndY=2.38342 EndZ=0
    g6: Circle [constr] CenterX=-48 CenterY=4 CenterZ=0 NormalX=0 NormalY=0 NormalZ=1 AngleXU=0 Radius=3.23316
    g7: LineSegment StartX=-44.7 StartY=5.90526 StartZ=0 EndX=-48 EndY=7.81051 EndZ=0
    g8: LineSegment StartX=-48 StartY=7.81051 StartZ=0 EndX=-51.3 EndY=5.90526 EndZ=0
    g9: LineSegment StartX=-51.3 StartY=5.90526 StartZ=0 EndX=-51.3 EndY=2.09474 EndZ=0
    g10: LineSegment StartX=-51.3 StartY=2.09474 StartZ=0 EndX=-48 EndY=0.189488 EndZ=0
    g11: LineSegment StartX=-48 StartY=0.189488 StartZ=0 EndX=-44.7 EndY=2.09474 EndZ=0
    g12: LineSegment StartX=-44.7 StartY=2.09474 StartZ=0 EndX=-44.7 EndY=5.90526 EndZ=0
    g13: Circle [constr] CenterX=-48 CenterY=4 CenterZ=0 NormalX=0 NormalY=0 NormalZ=1 AngleXU=0 Radius=3.81051
    g14: LineSegment StartX=16.8 StartY=43.3834 StartZ=0 EndX=16.8 EndY=46.6166 EndZ=0
    g15: LineSegment StartX=16.8 StartY=46.6166 StartZ=0 EndX=14 EndY=48.2332 EndZ=0
    g16: LineSegment StartX=14 StartY=48.2332 StartZ=0 EndX=11.2 EndY=46.6166 EndZ=0
    g17: LineSegment StartX=11.2 StartY=46.6166 StartZ=0 EndX=11.2 EndY=43.3834 EndZ=0
    g18: LineSegment StartX=11.2 StartY=43.3834 StartZ=0 EndX=14 EndY=41.7668 EndZ=0
    g19: LineSegment StartX=14 StartY=41.7668 StartZ=0 EndX=16.8 EndY=43.3834 EndZ=0
    g20: Circle [constr] CenterX=14 CenterY=45 CenterZ=0 NormalX=0 NormalY=0 NormalZ=1 AngleXU=0 Radius=3.23316
    g21: LineSegment StartX=17.3 StartY=46.9053 StartZ=0 EndX=14 EndY=48.8105 EndZ=0
    g22: LineSegment StartX=14 StartY=48.8105 StartZ=0 EndX=10.7 EndY=46.9053 EndZ=0
    g23: LineSegment StartX=10.7 StartY=46.9053 StartZ=0 EndX=10.7 EndY=43.0947 EndZ=0
    g24: LineSegment StartX=10.7 StartY=43.0947 StartZ=0 EndX=14 EndY=41.1895 EndZ=0
    g25: LineSegment StartX=14 StartY=41.1895 StartZ=0 EndX=17.3 EndY=43.0947 EndZ=0
    g26: LineSegment StartX=17.3 StartY=43.0947 StartZ=0 EndX=17.3 EndY=46.9053 EndZ=0
    g27: Circle [constr] CenterX=14 CenterY=45 CenterZ=0 NormalX=0 NormalY=0 NormalZ=1 AngleXU=0 Radius=3.81051
    g28: LineSegment StartX=-12.2 StartY=-0.616581 StartZ=0 EndX=-12.2 EndY=2.61658 EndZ=0
    g29: LineSegment StartX=-12.2 StartY=2.61658 StartZ=0 EndX=-15 EndY=4.23316 EndZ=0
    g30: LineSegment StartX=-15 StartY=4.23316 StartZ=0 EndX=-17.8 EndY=2.61658 EndZ=0
    g31: LineSegment StartX=-17.8 StartY=2.61658 StartZ=0 EndX=-17.8 EndY=-0.616581 EndZ=0
    g32: LineSegment StartX=-17.8 StartY=-0.616581 StartZ=0 EndX=-15 EndY=-2.23316 EndZ=0
    g33: LineSegment StartX=-15 StartY=-2.23316 StartZ=0 EndX=-12.2 EndY=-0.616581 EndZ=0
    g34: Circle [constr] CenterX=-15 CenterY=1 CenterZ=0 NormalX=0 NormalY=0 NormalZ=1 AngleXU=0 Radius=3.23316
    g35: LineSegment StartX=-11.7 StartY=2.90526 StartZ=0 EndX=-15 EndY=4.81051 EndZ=0
    g36: LineSegment StartX=-15 StartY=4.81051 StartZ=0 EndX=-18.3 EndY=2.90526 EndZ=0
    g37: LineSegment StartX=-18.3 StartY=2.90526 StartZ=0 EndX=-18.3 EndY=-0.905256 EndZ=0
    g38: LineSegment StartX=-18.3 StartY=-0.905256 StartZ=0 EndX=-15 EndY=-2.81051 EndZ=0
    g39: LineSegment StartX=-15 StartY=-2.81051 StartZ=0 EndX=-11.7 EndY=-0.905256 EndZ=0
    g40: LineSegment StartX=-11.7 StartY=-0.905256 StartZ=0 EndX=-11.7 EndY=2.90526 EndZ=0
    g41: Circle [constr] CenterX=-15 CenterY=1 CenterZ=0 NormalX=0 NormalY=0 NormalZ=1 AngleXU=0 Radius=3.81051
    g42: LineSegment StartX=50.8 StartY=2.38342 StartZ=0 EndX=50.8 EndY=5.61658 EndZ=0
    g43: LineSegment StartX=50.8 StartY=5.61658 StartZ=0 EndX=48 EndY=7.23316 EndZ=0
    g44: LineSegment StartX=48 StartY=7.23316 StartZ=0 EndX=45.2 EndY=5.61658 EndZ=0
    g45: LineSegment StartX=45.2 StartY=5.61658 StartZ=0 EndX=45.2 EndY=2.38342 EndZ=0
    g46: LineSegment StartX=45.2 StartY=2.38342 StartZ=0 EndX=48 EndY=0.766838 EndZ=0
    g47: LineSegment StartX=48 StartY=0.766838 StartZ=0 EndX=50.8 EndY=2.38342 EndZ=0
    g48: Circle [constr] CenterX=48 CenterY=4 CenterZ=0 NormalX=0 NormalY=0 NormalZ=1 AngleXU=0 Radius=3.23316
    g49: LineSegment StartX=51.3 StartY=5.90526 StartZ=0 EndX=48 EndY=7.81051 EndZ=0
    g50: LineSegment StartX=48 StartY=7.81051 StartZ=0 EndX=44.7 EndY=5.90526 EndZ=0
    g51: LineSegment StartX=44.7 StartY=5.90526 StartZ=0 EndX=44.7 EndY=2.09474 EndZ=0
    g52: LineSegment StartX=44.7 StartY=2.09474 StartZ=0 EndX=48 EndY=0.189488 EndZ=0
    g53: LineSegment StartX=48 StartY=0.189488 StartZ=0 EndX=51.3 EndY=2.09474 EndZ=0
    g54: LineSegment StartX=51.3 StartY=2.09474 StartZ=0 EndX=51.3 EndY=5.90526 EndZ=0
    g55: Circle [constr] CenterX=48 CenterY=4 CenterZ=0 NormalX=0 NormalY=0 NormalZ=1 AngleXU=0 Radius=3.81051
    g56: LineSegment StartX=17.8 StartY=-0.616581 StartZ=0 EndX=17.8 EndY=2.61658 EndZ=0
    g57: LineSegment StartX=17.8 StartY=2.61658 StartZ=0 EndX=15 EndY=4.23316 EndZ=0
    g58: LineSegment StartX=15 StartY=4.23316 StartZ=0 EndX=12.2 EndY=2.61658 EndZ=0
    g59: LineSegment StartX=12.2 StartY=2.61658 StartZ=0 EndX=12.2 EndY=-0.616581 EndZ=0
    g60: LineSegment StartX=12.2 StartY=-0.616581 StartZ=0 EndX=15 EndY=-2.23316 EndZ=0
    g61: LineSegment StartX=15 StartY=-2.23316 StartZ=0 EndX=17.8 EndY=-0.616581 EndZ=0
    g62: Circle [constr] CenterX=15 CenterY=1 CenterZ=0 NormalX=0 NormalY=0 NormalZ=1 AngleXU=0 Radius=3.23316
    g63: LineSegment StartX=18.3 StartY=2.90526 StartZ=0 EndX=15 EndY=4.81051 EndZ=0
    g64: LineSegment StartX=15 StartY=4.81051 StartZ=0 EndX=11.7 EndY=2.90526 EndZ=0
    g65: LineSegment StartX=11.7 StartY=2.90526 StartZ=0 EndX=11.7 EndY=-0.905256 EndZ=0
    g66: LineSegment StartX=11.7 StartY=-0.905256 StartZ=0 EndX=15 EndY=-2.81051 EndZ=0
    g67: LineSegment StartX=15 StartY=-2.81051 StartZ=0 EndX=18.3 EndY=-0.905256 EndZ=0
    g68: LineSegment StartX=18.3 StartY=-0.905256 StartZ=0 EndX=18.3 EndY=2.90526 EndZ=0
    g69: Circle [constr] CenterX=15 CenterY=1 CenterZ=0 NormalX=0 NormalY=0 NormalZ=1 AngleXU=0 Radius=3.81051
    g70: LineSegment StartX=50.8 StartY=-39.6166 StartZ=0 EndX=50.8 EndY=-36.3834 EndZ=0
    g71: LineSegment StartX=50.8 StartY=-36.3834 StartZ=0 EndX=48 EndY=-34.7668 EndZ=0
    g72: LineSegment StartX=48 StartY=-34.7668 StartZ=0 EndX=45.2 EndY=-36.3834 EndZ=0
    g73: LineSegment StartX=45.2 StartY=-36.3834 StartZ=0 EndX=45.2 EndY=-39.6166 EndZ=0
    g74: LineSegment StartX=45.2 StartY=-39.6166 StartZ=0 EndX=48 EndY=-41.2332 EndZ=0
    g75: LineSegment StartX=48 StartY=-41.2332 StartZ=0 EndX=50.8 EndY=-39.6166 EndZ=0
    g76: Circle [constr] CenterX=48 CenterY=-38 CenterZ=0 NormalX=0 NormalY=0 NormalZ=1 AngleXU=0 Radius=3.23316
    g77: LineSegment StartX=51.3 StartY=-36.0947 StartZ=0 EndX=48 EndY=-34.1895 EndZ=0
    g78: LineSegment StartX=48 StartY=-34.1895 StartZ=0 EndX=44.7 EndY=-36.0947 EndZ=0
    g79: LineSegment StartX=44.7 StartY=-36.0947 StartZ=0 EndX=44.7 EndY=-39.9053 EndZ=0
    g80: LineSegment StartX=44.7 StartY=-39.9053 StartZ=0 EndX=48 EndY=-41.8105 EndZ=0
    g81: LineSegment StartX=48 StartY=-41.8105 StartZ=0 EndX=51.3 EndY=-39.9053 EndZ=0
    g82: LineSegment StartX=51.3 StartY=-39.9053 StartZ=0 EndX=51.3 EndY=-36.0947 EndZ=0
    g83: Circle [constr] CenterX=48 CenterY=-38 CenterZ=0 NormalX=0 NormalY=0 NormalZ=1 AngleXU=0 Radius=3.81051
    g84: LineSegment StartX=-11.2 StartY=43.3834 StartZ=0 EndX=-11.2 EndY=46.6166 EndZ=0
    g85: LineSegment StartX=-11.2 StartY=46.6166 StartZ=0 EndX=-14 EndY=48.2332 EndZ=0
    g86: LineSegment StartX=-14 StartY=48.2332 StartZ=0 EndX=-16.8 EndY=46.6166 EndZ=0
    g87: LineSegment StartX=-16.8 StartY=46.6166 StartZ=0 EndX=-16.8 EndY=43.3834 EndZ=0
    g88: LineSegment StartX=-16.8 StartY=43.3834 StartZ=0 EndX=-14 EndY=41.7668 EndZ=0
    g89: LineSegment StartX=-14 StartY=41.7668 StartZ=0 EndX=-11.2 EndY=43.3834 EndZ=0
    g90: Circle [constr] CenterX=-14 CenterY=45 CenterZ=0 NormalX=0 NormalY=0 NormalZ=1 AngleXU=0 Radius=3.23316
    g91: LineSegment StartX=-10.7 StartY=46.9053 StartZ=0 EndX=-14 EndY=48.8105 EndZ=0
    g92: LineSegment StartX=-14 StartY=48.8105 StartZ=0 EndX=-17.3 EndY=46.9053 EndZ=0
    g93: LineSegment StartX=-17.3 StartY=46.9053 StartZ=0 EndX=-17.3 EndY=43.0947 EndZ=0
    g94: LineSegment StartX=-17.3 StartY=43.0947 StartZ=0 EndX=-14 EndY=41.1895 EndZ=0
    g95: LineSegment StartX=-14 StartY=41.1895 StartZ=0 EndX=-10.7 EndY=43.0947 EndZ=0
    g96: LineSegment StartX=-10.7 StartY=43.0947 StartZ=0 EndX=-10.7 EndY=46.9053 EndZ=0
    g97: Circle [constr] CenterX=-14 CenterY=45 CenterZ=0 NormalX=0 NormalY=0 NormalZ=1 AngleXU=0 Radius=3.81051
    g98: LineSegment StartX=-30.2 StartY=-45.6166 StartZ=0 EndX=-30.2 EndY=-42.3834 EndZ=0
    g99: LineSegment StartX=-30.2 StartY=-42.3834 StartZ=0 EndX=-33 EndY=-40.7668 EndZ=0
    g100: LineSegment StartX=-33 StartY=-40.7668 StartZ=0 EndX=-35.8 EndY=-42.3834 EndZ=0
    g101: LineSegment StartX=-35.8 StartY=-42.3834 StartZ=0 EndX=-35.8 EndY=-45.6166 EndZ=0
    g102: LineSegment StartX=-35.8 StartY=-45.6166 StartZ=0 EndX=-33 EndY=-47.2332 EndZ=0
    g103: LineSegment StartX=-33 StartY=-47.2332 StartZ=0 EndX=-30.2 EndY=-45.6166 EndZ=0
    g104: Circle [constr] CenterX=-33 CenterY=-44 CenterZ=0 NormalX=0 NormalY=0 NormalZ=1 AngleXU=0 Radius=3.23316
    g105: LineSegment StartX=-29.7 StartY=-42.0947 StartZ=0 EndX=-33 EndY=-40.1895 EndZ=0
    g106: LineSegment StartX=-33 StartY=-40.1895 StartZ=0 EndX=-36.3 EndY=-42.0947 EndZ=0
    g107: LineSegment StartX=-36.3 StartY=-42.0947 StartZ=0 EndX=-36.3 EndY=-45.9053 EndZ=0
    g108: LineSegment StartX=-36.3 StartY=-45.9053 StartZ=0 EndX=-33 EndY=-47.8105 EndZ=0
    g109: LineSegment StartX=-33 StartY=-47.8105 StartZ=0 EndX=-29.7 EndY=-45.9053 EndZ=0
    g110: LineSegment StartX=-29.7 StartY=-45.9053 StartZ=0 EndX=-29.7 EndY=-42.0947 EndZ=0
    g111: Circle [constr] CenterX=-33 CenterY=-44 CenterZ=0 NormalX=0 NormalY=0 NormalZ=1 AngleXU=0 Radius=3.81051
    g112: LineSegment StartX=35.8 StartY=-45.6166 StartZ=0 EndX=35.8 EndY=-42.3834 EndZ=0
    g113: LineSegment StartX=35.8 StartY=-42.3834 StartZ=0 EndX=33 EndY=-40.7668 EndZ=0
    g114: LineSegment StartX=33 StartY=-40.7668 StartZ=0 EndX=30.2 EndY=-42.3834 EndZ=0
    g115: LineSegment StartX=30.2 StartY=-42.3834 StartZ=0 EndX=30.2 EndY=-45.6166 EndZ=0
    g116: LineSegment StartX=30.2 StartY=-45.6166 StartZ=0 EndX=33 EndY=-47.2332 EndZ=0
    g117: LineSegment StartX=33 StartY=-47.2332 StartZ=0 EndX=35.8 EndY=-45.6166 EndZ=0
    g118: Circle [constr] CenterX=33 CenterY=-44 CenterZ=0 NormalX=0 NormalY=0 NormalZ=1 AngleXU=0 Radius=3.23316
    g119: LineSegment StartX=36.3 StartY=-42.0947 StartZ=0 EndX=33 EndY=-40.1895 EndZ=0
    g120: LineSegment StartX=33 StartY=-40.1895 StartZ=0 EndX=29.7 EndY=-42.0947 EndZ=0
    g121: LineSegment StartX=29.7 StartY=-42.0947 StartZ=0 EndX=29.7 EndY=-45.9053 EndZ=0
    g122: LineSegment StartX=29.7 StartY=-45.9053 StartZ=0 EndX=33 EndY=-47.8105 EndZ=0
    g123: LineSegment StartX=33 StartY=-47.8105 StartZ=0 EndX=36.3 EndY=-45.9053 EndZ=0
    g124: LineSegment StartX=36.3 StartY=-45.9053 StartZ=0 EndX=36.3 EndY=-42.0947 EndZ=0
    g125: Circle [constr] CenterX=33 CenterY=-44 CenterZ=0 NormalX=0 NormalY=0 NormalZ=1 AngleXU=0 Radius=3.81051
    g126: LineSegment StartX=-45.2 StartY=-39.6166 StartZ=0 EndX=-45.2 EndY=-36.3834 EndZ=0
    g127: LineSegment StartX=-45.2 StartY=-36.3834 StartZ=0 EndX=-48 EndY=-34.7668 EndZ=0
    g128: LineSegment StartX=-48 StartY=-34.7668 StartZ=0 EndX=-50.8 EndY=-36.3834 EndZ=0
    g129: LineSegment StartX=-50.8 StartY=-36.3834 StartZ=0 EndX=-50.8 EndY=-39.6166 EndZ=0
    g130: LineSegment StartX=-50.8 StartY=-39.6166 StartZ=0 EndX=-48 EndY=-41.2332 EndZ=0
    g131: LineSegment StartX=-48 StartY=-41.2332 StartZ=0 EndX=-45.2 EndY=-39.6166 EndZ=0
    g132: Circle [constr] CenterX=-48 CenterY=-38 CenterZ=0 NormalX=0 NormalY=0 NormalZ=1 AngleXU=0 Radius=3.23316
    g133: LineSegment StartX=-44.7 StartY=-36.0947 StartZ=0 EndX=-48 EndY=-34.1895 EndZ=0
    g134: LineSegment StartX=-48 StartY=-34.1895 StartZ=0 EndX=-51.3 EndY=-36.0947 EndZ=0
    g135: LineSegment StartX=-51.3 StartY=-36.0947 StartZ=0 EndX=-51.3 EndY=-39.9053 EndZ=0
    g136: LineSegment StartX=-51.3 StartY=-39.9053 StartZ=0 EndX=-48 EndY=-41.8105 EndZ=0
    g137: LineSegment StartX=-48 StartY=-41.8105 StartZ=0 EndX=-44.7 EndY=-39.9053 EndZ=0
    g138: LineSegment StartX=-44.7 StartY=-39.9053 StartZ=0 EndX=-44.7 EndY=-36.0947 EndZ=0
    g139: Circle [constr] CenterX=-48 CenterY=-38 CenterZ=0 NormalX=0 NormalY=0 NormalZ=1 AngleXU=0 Radius=3.81051
  constraints (320):
    c: Coincident(g0,g1)
    c: Coincident(g1,g2)
    c: Coincident(g2,g3)
    c: Coincident(g3,g4)
    c: Coincident(g4,g5)
    c: Coincident(g5,g0)
    c: Equal(g0, g1-g5) x5
    c: PointOnObject(g0,g6)
    c: PointOnObject(g1,g6)
    c: PointOnObject(g2,g6)
    c: PointOnObject(g3,g6)
    c: PointOnObject(g4,g6)
    c: PointOnObject(g5,g6)
    c: Vertical(g0)
    c: DistanceX(g2,g0) = 5.6
    c: Coincident(g7,g8)
    c: Coincident(g8,g9)
    c: Coincident(g9,g10)
    c: Coincident(g10,g11)
    c: Coincident(g11,g12)
    c: Coincident(g12,g7)
    c: Equal(g7, g8-g12) x5
    c: PointOnObject(g7,g13)
    c: PointOnObject(g8,g13)
    c: PointOnObject(g9,g13)
    c: PointOnObject(g10,g13)
    c: PointOnObject(g11,g13)
    c: PointOnObject(g12,g13)
    c: Coincident(g13,g6)
    c: Vertical(g12)
    c: DistanceX(g0,g7) = 0.5
    c: Coincident(g14,g15)
    c: Coincident(g15,g16)
    c: Coincident(g16,g17)
    c: Coincident(g17,g18)
    c: Coincident(g18,g19)
    c: Coincident(g19,g14)
    c: Equal(g14, g15-g19) x5
    c: PointOnObject(g14,g20)
    c: PointOnObject(g15,g20)
    c: PointOnObject(g16,g20)
    c: PointOnObject(g17,g20)
    c: PointOnObject(g18,g20)
    c: PointOnObject(g19,g20)
    c: Vertical(g14)
    c: DistanceX(g16,g14) = 5.6
    c: Coincident(g21,g22)
    c: Coincident(g22,g23)
    c: Coincident(g23,g24)
    c: Coincident(g24,g25)
    c: Coincident(g25,g26)
    c: Coincident(g26,g21)
    c: Equal(g21, g22-g26) x5
    c: PointOnObject(g21,g27)
    c: PointOnObject(g22,g27)
    c: PointOnObject(g23,g27)
    c: PointOnObject(g24,g27)
    c: PointOnObject(g25,g27)
    c: PointOnObject(g26,g27)
    c: Coincident(g27,g20)
    c: Vertical(g26)
    c: DistanceX(g14,g21) = 0.5
    c: Coincident(g28,g29)
    c: Coincident(g29,g30)
    c: Coincident(g30,g31)
    c: Coincident(g31,g32)
    c: Coincident(g32,g33)
    c: Coincident(g33,g28)
    c: Equal(g28, g29-g33) x5
    c: PointOnObject(g28,g34)
    c: PointOnObject(g29,g34)
    c: PointOnObject(g30,g34)
    c: PointOnObject(g31,g34)
    c: PointOnObject(g32,g34)
    c: PointOnObject(g33,g34)
    c: Vertical(g28)
    c: DistanceX(g30,g28) = 5.6
    c: Coincident(g35,g36)
    c: Coincident(g36,g37)
    c: Coincident(g37,g38)
    c: Coincident(g38,g39)
    c: Coincident(g39,g40)
    c: Coincident(g40,g35)
    c: Equal(g35, g36-g40) x5
    c: PointOnObject(g35,g41)
    c: PointOnObject(g36,g41)
    c: PointOnObject(g37,g41)
    c: PointOnObject(g38,g41)
    c: PointOnObject(g39,g41)
    c: PointOnObject(g40,g41)
    c: Coincident(g41,g34)
    c: Vertical(g40)
    c: DistanceX(g28,g35) = 0.5
    c: Coincident(g42,g43)
    c: Coincident(g43,g44)
    c: Coincident(g44,g45)
    c: Coincident(g45,g46)
    c: Coincident(g46,g47)
    c: Coincident(g47,g42)
    c: Equal(g42, g43-g47) x5
    c: PointOnObject(g42,g48)
    c: PointOnObject(g43,g48)
    c: PointOnObject(g44,g48)
    c: PointOnObject(g45,g48)
    c: PointOnObject(g46,g48)
    c: PointOnObject(g47,g48)
    c: Vertical(g42)
    c: DistanceX(g44,g42) = 5.6
    c: Coincident(g49,g50)
    c: Coincident(g50,g51)
    c: Coincident(g51,g52)
    c: Coincident(g52,g53)
    c: Coincident(g53,g54)
    c: Coincident(g54,g49)
    c: Equal(g49, g50-g54) x5
    c: PointOnObject(g49,g55)
    c: PointOnObject(g50,g55)
    c: PointOnObject(g51,g55)
    c: PointOnObject(g52,g55)
    c: PointOnObject(g53,g55)
    c: PointOnObject(g54,g55)
    c: Coincident(g55,g48)
    c: Vertical(g54)
    c: DistanceX(g42,g49) = 0.5
    c: Coincident(g56,g57)
    c: Coincident(g57,g58)
    c: Coincident(g58,g59)
    c: Coincident(g59,g60)
    c: Coincident(g60,g61)
    c: Coincident(g61,g56)
    c: Equal(g56, g57-g61) x5
    c: PointOnObject(g56,g62)
    c: PointOnObject(g57,g62)
    c: PointOnObject(g58,g62)
    c: PointOnObject(g59,g62)
    c: PointOnObject(g60,g62)
    c: PointOnObject(g61,g62)
    c: Vertical(g56)
    c: DistanceX(g58,g56) = 5.6
    c: Coincident(g63,g64)
    c: Coincident(g64,g65)
    c: Coincident(g65,g66)
    c: Coincident(g66,g67)
    c: Coincident(g67,g68)
    c: Coincident(g68,g63)
    c: Equal(g63, g64-g68) x5
    c: PointOnObject(g63,g69)
    c: PointOnObject(g64,g69)
    c: PointOnObject(g65,g69)
    c: PointOnObject(g66,g69)
    c: PointOnObject(g67,g69)
    c: PointOnObject(g68,g69)
    c: Coincident(g69,g62)
    c: Vertical(g68)
    c: DistanceX(g56,g63) = 0.5
    c: Coincident(g70,g71)
    c: Coincident(g71,g72)
    c: Coincident(g72,g73)
    c: Coincident(g73,g74)
    c: Coincident(g74,g75)
    c: Coincident(g75,g70)
    c: Equal(g70, g71-g75) x5
    c: PointOnObject(g70,g76)
    c: PointOnObject(g71,g76)
    c: PointOnObject(g72,g76)
    c: PointOnObject(g73,g76)
    c: PointOnObject(g74,g76)
    c: PointOnObject(g75,g76)
    c: Vertical(g70)
    c: DistanceX(g72,g70) = 5.6
    c: Coincident(g77,g78)
    c: Coincident(g78,g79)
    c: Coincident(g79,g80)
    c: Coincident(g80,g81)
    c: Coincident(g81,g82)
    c: Coincident(g82,g77)
    c: Equal(g77, g78-g82) x5
    c: PointOnObject(g77,g83)
    c: PointOnObject(g78,g83)
    c: PointOnObject(g79,g83)
    c: PointOnObject(g80,g83)
    c: PointOnObject(g81,g83)
    c: PointOnObject(g82,g83)
    c: Coincident(g83,g76)
    c: Vertical(g82)
    c: DistanceX(g70,g77) = 0.5
    c: Coincident(g84,g85)
    c: Coincident(g85,g86)
    c: Coincident(g86,g87)
    c: Coincident(g87,g88)
    c: Coincident(g88,g89)
    c: Coincident(g89,g84)
    c: Equal(g84, g85-g89) x5
    c: PointOnObject(g84,g90)
    c: PointOnObject(g85,g90)
    c: PointOnObject(g86,g90)
    c: PointOnObject(g87,g90)
    c: PointOnObject(g88,g90)
    c: PointOnObject(g89,g90)
    c: Vertical(g84)
    c: DistanceX(g86,g84) = 5.6
    c: Coincident(g91,g92)
    c: Coincident(g92,g93)
    c: Coincident(g93,g94)
    c: Coincident(g94,g95)
    c: Coincident(g95,g96)
    c: Coincident(g96,g91)
    c: Equal(g91, g92-g96) x5
    c: PointOnObject(g91,g97)
    c: PointOnObject(g92,g97)
    c: PointOnObject(g93,g97)
    c: PointOnObject(g94,g97)
    c: PointOnObject(g95,g97)
    c: PointOnObject(g96,g97)
    c: Coincident(g97,g90)
    c: Vertical(g96)
    c: DistanceX(g84,g91) = 0.5
    c: Coincident(g98,g99)
    c: Coincident(g99,g100)
    c: Coincident(g100,g101)
    c: Coincident(g101,g102)
    c: Coincident(g102,g103)
    c: Coincident(g103,g98)
    c: Equal(g98, g99-g103) x5
    c: PointOnObject(g98,g104)
    c: PointOnObject(g99,g104)
    c: PointOnObject(g100,g104)
    c: PointOnObject(g101,g104)
    c: PointOnObject(g102,g104)
    c: PointOnObject(g103,g104)
    c: Vertical(g98)
    c: DistanceX(g100,g98) = 5.6
    c: Coincident(g105,g106)
    c: Coincident(g106,g107)
    c: Coincident(g107,g108)
    c: Coincident(g108,g109)
    c: Coincident(g109,g110)
    c: Coincident(g110,g105)
    c: Equal(g105, g106-g110) x5
    c: PointOnObject(g105,g111)
    c: PointOnObject(g106,g111)
    c: PointOnObject(g107,g111)
    c: PointOnObject(g108,g111)
    c: PointOnObject(g109,g111)
    c: PointOnObject(g110,g111)
    c: Coincident(g111,g104)
    c: Vertical(g110)
    c: DistanceX(g98,g105) = 0.5
    c: Coincident(g112,g113)
    c: Coincident(g113,g114)
    c: Coincident(g114,g115)
    c: Coincident(g115,g116)
    c: Coincident(g116,g117)
    c: Coincident(g117,g112)
    c: Equal(g112, g113-g117) x5
    c: PointOnObject(g112,g118)
    c: PointOnObject(g113,g118)
    c: PointOnObject(g114,g118)
    c: PointOnObject(g115,g118)
    c: PointOnObject(g116,g118)
    c: PointOnObject(g117,g118)
    c: Vertical(g112)
    c: DistanceX(g114,g112) = 5.6
    c: Coincident(g119,g120)
    c: Coincident(g120,g121)
    c: Coincident(g121,g122)
    c: Coincident(g122,g123)
    c: Coincident(g123,g124)
    c: Coincident(g124,g119)
    c: Equal(g119, g120-g124) x5
    c: PointOnObject(g119,g125)
    c: PointOnObject(g120,g125)
    c: PointOnObject(g121,g125)
    c: PointOnObject(g122,g125)
    c: PointOnObject(g123,g125)
    c: PointOnObject(g124,g125)
    c: Coincident(g125,g118)
    c: Vertical(g124)
    c: DistanceX(g112,g119) = 0.5
    c: Coincident(g20,g-4)
    c: Coincident(g48,g-7)
    c: Coincident(g62,g-6)
    c: Coincident(g34,g-5)
    c: Coincident(g6,g-3)
    c: Coincident(g76,g-11)
    c: Coincident(g126,g127)
    c: Coincident(g127,g128)
    c: Coincident(g128,g129)
    c: Coincident(g129,g130)
    c: Coincident(g130,g131)
    c: Coincident(g131,g126)
    c: Equal(g126, g127-g131) x5
    c: PointOnObject(g126,g132)
    c: PointOnObject(g127,g132)
    c: PointOnObject(g128,g132)
    c: PointOnObject(g129,g132)
    c: PointOnObject(g130,g132)
    c: PointOnObject(g131,g132)
    c: Vertical(g126)
    c: DistanceX(g128,g126) = 5.6
    c: Coincident(g133,g134)
    c: Coincident(g134,g135)
    c: Coincident(g135,g136)
    c: Coincident(g136,g137)
    c: Coincident(g137,g138)
    c: Coincident(g138,g133)
    c: Equal(g133, g134-g138) x5
    c: PointOnObject(g133,g139)
    c: PointOnObject(g134,g139)
    c: PointOnObject(g135,g139)
    c: PointOnObject(g136,g139)
    c: PointOnObject(g137,g139)
    c: PointOnObject(g138,g139)
    c: Coincident(g139,g132)
    c: Vertical(g138)
    c: DistanceX(g126,g133) = 0.5
    c: Coincident(g90,g-12)
    c: Coincident(g118,g-10)
    c: Coincident(g-9,g104)
    c: Coincident(g132,g-8)
FEATURE [PartDesign::Pad] Pad347
  BaseFeature = -> Pocket208
  Length = 0.6
  Length2 = 100
  Profile = -> Sketch799
  Reversed = true
  Type = 0
FEATURE [PartDesign::LinearPattern] LinearPattern001
  BaseFeature = -> Pad347
  Direction = -> Sketch787 [N_Axis]
  Length = 21
  Occurrences = 2
  Originals = -> [Pocket208]
FEATURE [Sketcher::SketchObject] Sketch807
  AttachmentOffset = pos=(0,0,6) rot=(0,0,1;0rad)
  MapMode = 5
  Placement = pos=(0,0,6) rot=(0,0,1;0rad)
  Support = -> [XY_Plane027]
  sketch-geometry (8):
    g0: LineSegment StartX=-29.5162 StartY=-32.25 StartZ=0 EndX=-2.3459 EndY=-32.25 EndZ=0
    g1: LineSegment StartX=-2.3459 StartY=-32.25 StartZ=0 EndX=-2.3459 EndY=-44.111 EndZ=0
    g2: LineSegment StartX=-2.3459 StartY=-44.111 StartZ=0 EndX=-29.5162 EndY=-44.111 EndZ=0
    g3: LineSegment StartX=-29.5162 StartY=-44.111 StartZ=0 EndX=-29.5162 EndY=-32.25 EndZ=0
    g4: LineSegment StartX=2.3459 StartY=-32.25 StartZ=0 EndX=29.5162 EndY=-32.25 EndZ=0
    g5: LineSegment StartX=29.5162 StartY=-32.25 StartZ=0 EndX=29.5162 EndY=-44.111 EndZ=0
    g6: LineSegment StartX=29.5162 StartY=-44.111 StartZ=0 EndX=2.3459 EndY=-44.111 EndZ=0
    g7: LineSegment StartX=2.3459 StartY=-44.111 StartZ=0 EndX=2.3459 EndY=-32.25 EndZ=0
  constraints (17):
    c: Coincident(g0,g1)
    c: Coincident(g1,g2)
    c: Coincident(g2,g3)
    c: Coincident(g3,g0)
    c: Horizontal(g0)
    c: Horizontal(g2)
    c: Vertical(g1)
    c: Vertical(g3)
    c: Coincident(g4,g5)
    c: Coincident(g5,g6)
    c: Coincident(g6,g7)
    c: Coincident(g7,g4)
    c: Horizontal(g4)
    c: Vertical(g5)
    c: Symmetric(g0,g4,g-2)
    c: Symmetric(g1,g6,g-2)
    c: Symmetric(g2,g5,g-2)
FEATURE [PartDesign::Pocket] Pocket220
  BaseFeature = -> LinearPattern001
  Length = 2
  Length2 = 100
  Profile = -> Sketch807
  Type = 0
FEATURE [Sketcher::SketchObject] Sketch810
  MapMode = 5
  Support = -> [XY_Plane027]
  sketch-geometry (2):
    g0: Circle CenterX=-28 CenterY=-28 CenterZ=0 NormalX=0 NormalY=0 NormalZ=1 AngleXU=0 Radius=1.8
    g1: Circle CenterX=28 CenterY=-28 CenterZ=0 NormalX=0 NormalY=0 NormalZ=1 AngleXU=0 Radius=1.8
  constraints (5):
    c: DistanceX(g0) = -28
    c: DistanceY(g0) = -28
    c: Symmetric(g0,g1,g-2)
    c: Diameter(g0) = 3.6
    c: Equal(g0,g1)
FEATURE [PartDesign::Pocket] Pocket221
  BaseFeature = -> Pocket220
  Length = 5
  Length2 = 100
  Midplane = true
  Profile = -> Sketch810
  Type = 1
FEATURE [Sketcher::SketchObject] Sketch811
  AttachmentOffset = pos=(0,0,4) rot=(0,0,1;0rad)
  ExternalGeometry = -> [Sketch810]
  MapMode = 5
  Placement = pos=(0,0,4) rot=(0,0,1;0rad)
  Support = -> [XY_Plane027]
  sketch-geometry (14):
    g0: LineSegment StartX=30.8 StartY=-29.6166 StartZ=0 EndX=30.8 EndY=-26.3834 EndZ=0
    g1: LineSegment StartX=30.8 StartY=-26.3834 StartZ=0 EndX=28 EndY=-24.7668 EndZ=0
    g2: LineSegment StartX=28 StartY=-24.7668 StartZ=0 EndX=25.2 EndY=-26.3834 EndZ=0
    g3: LineSegment StartX=25.2 StartY=-26.3834 StartZ=0 EndX=25.2 EndY=-29.6166 EndZ=0
    g4: LineSegment StartX=25.2 StartY=-29.6166 StartZ=0 EndX=28 EndY=-31.2332 EndZ=0
    g5: LineSegment StartX=28 StartY=-31.2332 StartZ=0 EndX=30.8 EndY=-29.6166 EndZ=0
    g6: Circle [constr] CenterX=28 CenterY=-28 CenterZ=0 NormalX=0 NormalY=0 NormalZ=1 AngleXU=0 Radius=3.23316
    g7: LineSegment StartX=-25.2 StartY=-29.6166 StartZ=0 EndX=-25.2 EndY=-26.3834 EndZ=0
    g8: LineSegment StartX=-25.2 StartY=-26.3834 StartZ=0 EndX=-28 EndY=-24.7668 EndZ=0
    g9: LineSegment StartX=-28 StartY=-24.7668 StartZ=0 EndX=-30.8 EndY=-26.3834 EndZ=0
    g10: LineSegment StartX=-30.8 StartY=-26.3834 StartZ=0 EndX=-30.8 EndY=-29.6166 EndZ=0
    g11: LineSegment StartX=-30.8 StartY=-29.6166 StartZ=0 EndX=-28 EndY=-31.2332 EndZ=0
    g12: LineSegment StartX=-28 StartY=-31.2332 StartZ=0 EndX=-25.2 EndY=-29.6166 EndZ=0
    g13: Circle [constr] CenterX=-28 CenterY=-28 CenterZ=0 NormalX=0 NormalY=0 NormalZ=1 AngleXU=0 Radius=3.23316
  constraints (32):
    c: Coincident(g0,g1)
    c: Coincident(g1,g2)
    c: Coincident(g2,g3)
    c: Coincident(g3,g4)
    c: Coincident(g4,g5)
    c: Coincident(g5,g0)
    c: Equal(g0, g1-g5) x5
    c: PointOnObject(g0,g6)
    c: PointOnObject(g1,g6)
    c: PointOnObject(g2,g6)
    c: PointOnObject(g3,g6)
    c: PointOnObject(g4,g6)
    c: PointOnObject(g5,g6)
    c: Coincident(g6,g-3)
    c: Coincident(g7,g8)
    c: Coincident(g8,g9)
    c: Coincident(g9,g10)
    c: Coincident(g10,g11)
    c: Coincident(g11,g12)
    c: Coincident(g12,g7)
    c: Equal(g7, g8-g12) x5
    c: PointOnObject(g7,g13)
    c: PointOnObject(g8,g13)
    c: PointOnObject(g9,g13)
    c: PointOnObject(g10,g13)
    c: PointOnObject(g11,g13)
    c: PointOnObject(g12,g13)
    c: Coincident(g13,g-4)
    c: Vertical(g0)
    c: Vertical(g7)
    c: DistanceX(g2,g0) = 5.6
    c: Equal(g6,g13)
FEATURE [PartDesign::Pocket] Pocket222
  BaseFeature = -> Pocket221
  Length = 5
  Length2 = 100
  Profile = -> Sketch811
  Type = 0
FEATURE [PartDesign::Body] Body021  label="BodyL"
  Group = -> [Sketch290,Sketch001,Pad060,Sketch007,Pad016,Sketch020,Pad226,Sketch593,Pad227,Sketch594,Pad228,Pocket008,Sketch021,Pocket009,Sketch110,Pocket005,Pocket006,Sketch294,Pocket028,Sketch295,Pocket029,Sketch299,Pocket032,Sketch300,Pocket033,Sketch301,Pocket034,Sketch396,Sketch592,Pocket101,Sketch397,Pocket102,Sketch398,Pocket103,Sketch787,Pocket208,Sketch799,Pad347,LinearPattern001,Sketch807,Pocket220,+4 more]
  Origin = -> Origin027
  Placement = pos=(3.97809,6.58189,62) rot=(1,0,0;1.5708rad)
  Tip = -> Pocket222
FEATURE [Sketcher::SketchObject] Sketch
  MapMode = 5
  Placement = pos=(0,0,0) rot=(1,0,0;1.5708rad)
  Support = -> [XZ_Plane]
  sketch-geometry (22):
    g0: LineSegment StartX=17.1705 StartY=114.035 StartZ=0 EndX=29.0282 EndY=114.035 EndZ=0
    g1: LineSegment StartX=34.4207 StartY=109.455 StartZ=0 EndX=41.2491 EndY=67.8517 EndZ=0
    g2: LineSegment StartX=41.2491 StartY=67.8517 StartZ=0 EndX=44.4154 EndY=58.5663 EndZ=0
    g3: LineSegment StartX=48.3952 StartY=55.7185 StartZ=0 EndX=55.488 EndY=55.7185 EndZ=0
    g4: LineSegment StartX=59.5968 StartY=51.6098 StartZ=0 EndX=59.5968 EndY=41.694 EndZ=0
    g5: LineSegment StartX=59.7459 StartY=33.5121 StartZ=0 EndX=60.6398 EndY=9 EndZ=0
    g6: LineSegment StartX=28 StartY=42 StartZ=0 EndX=25.8427 EndY=51.7837 EndZ=0
    g7: LineSegment StartX=24.5788 StartY=63.385 StartZ=0 EndX=24.5788 EndY=74.28 EndZ=0
    g8: LineSegment StartX=19.6311 StartY=84.2243 StartZ=0 EndX=15.4614 EndY=87.3773 EndZ=0
    g9: LineSegment StartX=12.1697 StartY=94.0577 StartZ=0 EndX=12.2862 EndY=109.188 EndZ=0
    g10: ArcOfCircle CenterX=17.1705 CenterY=109.151 CenterZ=0 NormalX=0 NormalY=0 NormalZ=1 AngleXU=0 Radius=4.88447 StartAngle=1.5708 EndAngle=3.13389
    g11: ArcOfCircle CenterX=29.0282 CenterY=108.57 CenterZ=0 NormalX=0 NormalY=0 NormalZ=1 AngleXU=0 Radius=5.46462 StartAngle=0.16268 EndAngle=1.5708
    g12: ArcOfCircle CenterX=20.4646 CenterY=93.9938 CenterZ=0 NormalX=0 NormalY=0 NormalZ=1 AngleXU=0 Radius=8.29519 StartAngle=3.13389 EndAngle=4.06495
    g13: ArcOfCircle CenterX=55.488 CenterY=51.6098 CenterZ=0 NormalX=0 NormalY=0 NormalZ=1 AngleXU=0 Radius=4.10879 StartAngle=4e-16 EndAngle=1.5708
    g14: ArcOfCircle CenterX=48.3952 CenterY=59.9234 CenterZ=0 NormalX=0 NormalY=0 NormalZ=1 AngleXU=0 Radius=4.20482 StartAngle=3.47022 EndAngle=4.71239
    g15: ArcOfCircle CenterX=78.4559 CenterY=63.385 CenterZ=0 NormalX=0 NormalY=0 NormalZ=1 AngleXU=0 Radius=53.8771 StartAngle=3.14159 EndAngle=3.35862
    g16: ArcOfCircle CenterX=12.1115 CenterY=74.28 CenterZ=0 NormalX=0 NormalY=0 NormalZ=1 AngleXU=0 Radius=12.4673 StartAngle=2e-16 EndAngle=0.923357
    g17: Circle CenterX=17.9616 CenterY=107.034 CenterZ=0 NormalX=0 NormalY=0 NormalZ=1 AngleXU=0 Radius=1.85
    g18: ArcOfCircle CenterX=284.118 CenterY=41.694 CenterZ=0 NormalX=0 NormalY=0 NormalZ=1 AngleXU=0 Radius=224.521 StartAngle=3.14159 EndAngle=3.17804
    g19: Circle CenterX=52.0196 CenterY=24.0385 CenterZ=0 NormalX=0 NormalY=0 NormalZ=1 AngleXU=0 Radius=1.85
    g20: LineSegment StartX=25 StartY=9 StartZ=0 EndX=60.6398 EndY=9 EndZ=0
    g21: LineSegment StartX=28 StartY=42 StartZ=0 EndX=25 EndY=9 EndZ=0
  constraints (26):
    c: Horizontal(g0)
    c: Coincident(g1,g2)
    c: Horizontal(g3)
    c: Vertical(g4)
    c: Vertical(g7)
    c: Tangent(g9,g10) = 1.5708
    c: Tangent(g0,g10) = 1.5708
    c: Tangent(g0,g11) = 1.5708
    c: Tangent(g1,g11) = 1.5708
    c: Tangent(g9,g12) = 1.5708
    c: Tangent(g8,g12) = 1.5708
    c: Tangent(g3,g13) = 1.5708
    c: Tangent(g4,g13) = 1.5708
    c: Tangent(g2,g14) = -1.5708
    c: Tangent(g3,g14) = -1.5708
    c: Tangent(g6,g15) = 1.5708
    c: Tangent(g7,g15) = 1.5708
    c: Tangent(g7,g16) = -1.5708
    c: Tangent(g8,g16) = -1.5708
    c: Diameter(g17) = 3.7
    c: Tangent(g4,g18) = -1.5708
    c: Tangent(g5,g18) = -1.5708
    c: Coincident(g20,g5)
    c: Horizontal(g20)
    c: Coincident(g6,g21)
    c: Coincident(g20,g21)
FEATURE [PartDesign::Pad] Pad
  Length = 3
  Length2 = 100
  Placement = pos=(0,0,0) rot=(1,0,0;1.5708rad)
  Profile = -> Sketch
  Type = 0
FEATURE [Sketcher::SketchObject] Sketch812
  AttachmentOffset = pos=(0,0,19) rot=(0,0,1;0rad)
  MapMode = 5
  Placement = pos=(0,0,19) rot=(0,0,1;0rad)
  Support = -> [XY_Plane]
  sketch-geometry (23):
    g0: Circle CenterX=17.4605 CenterY=-55 CenterZ=0 NormalX=0 NormalY=0 NormalZ=1 AngleXU=0 Radius=2.85
    g1: LineSegment StartX=35.3859 StartY=-0.616313 StartZ=0 EndX=31 EndY=-0.47951 EndZ=0
    g2: LineSegment StartX=56.8416 StartY=-0.616313 StartZ=0 EndX=35.3859 EndY=-0.616313 EndZ=0
    g3: LineSegment StartX=23.7336 StartY=-59.1856 StartZ=0 EndX=33.7816 EndY=-41.4103 EndZ=0
    g4: LineSegment StartX=31 StartY=-0.47951 StartZ=0 EndX=24.2452 EndY=-0.47951 EndZ=0
    g5: LineSegment StartX=24.2452 StartY=-0.47951 StartZ=0 EndX=17 EndY=-22 EndZ=0
    g6: LineSegment StartX=16.1601 StartY=-59.9083 StartZ=0 EndX=22.4948 EndY=-59.9083 EndZ=0
    g7: LineSegment StartX=10.684 StartY=-40.9625 StartZ=0 EndX=8.35233 EndY=-49.7622 EndZ=0
    g8: ArcOfCircle CenterX=16.1601 CenterY=-51.8311 CenterZ=0 NormalX=0 NormalY=0 NormalZ=1 AngleXU=0 Radius=8.07725 StartAngle=2.88257 EndAngle=4.71239
    g9: ArcOfCircle CenterX=22.4948 CenterY=-58.4853 CenterZ=0 NormalX=0 NormalY=0 NormalZ=1 AngleXU=0 Radius=1.42305 StartAngle=4.71239 EndAngle=5.76869
    g10: LineSegment StartX=17 StartY=-22 StartZ=0 EndX=18.7141 EndY=-22.7794 EndZ=0
    g11: LineSegment StartX=18.7141 StartY=-22.7794 StartZ=0 EndX=20.7 EndY=-23 EndZ=0
    g12: LineSegment StartX=20.7 StartY=-23 StartZ=0 EndX=26.4617 EndY=-26 EndZ=0
    g13: LineSegment StartX=26.4617 StartY=-26 StartZ=0 EndX=28 EndY=-30.7075 EndZ=0
    g14: LineSegment StartX=28 StartY=-30.7075 StartZ=0 EndX=27.5317 EndY=-36 EndZ=0
    g15: LineSegment StartX=27.5317 StartY=-36 StartZ=0 EndX=25 EndY=-40.3378 EndZ=0
    g16: LineSegment StartX=25 StartY=-40.3378 StartZ=0 EndX=20.6176 EndY=-43 EndZ=0
    g17: LineSegment StartX=20.6176 StartY=-43 StartZ=0 EndX=16.4198 EndY=-43.7125 EndZ=0
    g18: LineSegment StartX=16.4198 StartY=-43.7125 StartZ=0 EndX=12.222 EndY=-41.7371 EndZ=0
    g19: LineSegment StartX=12.222 StartY=-41.7371 StartZ=0 EndX=10.684 EndY=-40.9625 EndZ=0
    g20: LineSegment StartX=42.2719 StartY=-26.3907 StartZ=0 EndX=42.2054 EndY=-35.6693 EndZ=0
    g21: LineSegment StartX=42.2054 StartY=-35.6693 StartZ=0 EndX=33.7816 EndY=-41.4103 EndZ=0
    g22: LineSegment StartX=42.2719 StartY=-26.3907 StartZ=0 EndX=56.8416 EndY=-0.616313 EndZ=0
  constraints (28):
    c: Diameter(g0) = 5.7
    c: Coincident(g2,g1)
    c: Horizontal(g2)
    c: Coincident(g22,g2)
    c: Coincident(g1,g4)
    c: Horizontal(g4)
    c: Coincident(g4,g5)
    c: Horizontal(g6)
    c: DistanceY(g0,g-1) = 55
    c: Tangent(g7,g8) = -1.5708
    c: Tangent(g6,g8) = -1.5708
    c: Tangent(g6,g9) = -1.5708
    c: Tangent(g3,g9) = -1.5708
    c: Coincident(g5,g10)
    c: Coincident(g10,g11)
    c: Coincident(g11,g12)
    c: Coincident(g12,g13)
    c: Coincident(g13,g14)
    c: Coincident(g14,g15)
    c: Coincident(g15,g16)
    c: Coincident(g16,g17)
    c: Coincident(g17,g18)
    c: Coincident(g18,g19)
    c: Coincident(g19,g7)
    c: Coincident(g20,g21)
    c: Coincident(g3,g21)
    c: Coincident(g22,g20)
    c: Tangent(g3,g22)
FEATURE [PartDesign::Pad] Pad348
  BaseFeature = -> Pad
  Length = 10
  Length2 = 100
  Placement = pos=(0,0,0) rot=(1,0,0;1.5708rad)
  Profile = -> Sketch812
  Reversed = true
  Type = 0
FEATURE [Sketcher::SketchObject] Sketch813
  AttachmentOffset = pos=(0,0,90) rot=(0,0,1;0rad)
  MapMode = 5
  Placement = pos=(0,0,90) rot=(0,0,1;0rad)
  Support = -> [XY_Plane]
  sketch-geometry (26):
    g0: Circle CenterX=8 CenterY=-53.7078 CenterZ=0 NormalX=0 NormalY=0 NormalZ=1 AngleXU=0 Radius=3.51387
    g1: Circle CenterX=41.7955 CenterY=-53 CenterZ=0 NormalX=0 NormalY=0 NormalZ=1 AngleXU=0 Radius=3.58704
    g2: LineSegment StartX=18.1699 StartY=-0.624235 StartZ=0 EndX=26.3678 EndY=-19.0702 EndZ=0
    g3: LineSegment StartX=44.9142 StartY=-61.7997 StartZ=0 EndX=46.3183 EndY=-60.9233 EndZ=0
    g4: LineSegment StartX=51.0004 StartY=-51.3554 StartZ=0 EndX=48.6067 EndY=-28.1038 EndZ=0
    g5: LineSegment StartX=44.0315 StartY=-14.1809 StartZ=0 EndX=36.0446 EndY=-0.624235 EndZ=0
    g6: LineSegment StartX=36.0446 StartY=-0.624235 StartZ=0 EndX=18.1699 EndY=-0.624235 EndZ=0
    g7: LineSegment StartX=14.7825 StartY=-59.7349 StartZ=0 EndX=16.395 EndY=-55.344 EndZ=0
    g8: LineSegment StartX=16.4513 StartY=-55.1625 StartZ=0 EndX=16.6223 EndY=-54.4915 EndZ=0
    g9: LineSegment StartX=26.4937 StartY=-49.5602 StartZ=0 EndX=28.7912 EndY=-50.5173 EndZ=0
    g10: LineSegment StartX=35.7365 StartY=-57.4158 StartZ=0 EndX=36.4658 EndY=-59.1338 EndZ=0
    g11: LineSegment StartX=27.333 StartY=-21.6439 StartZ=0 EndX=28.6317 EndY=-25.8505 EndZ=0
    g12: LineSegment StartX=24.3572 StartY=-36.0031 StartZ=0 EndX=8.40281 EndY=-44.1951 EndZ=0
    g13: LineSegment StartX=1.90513 StartY=-51.7194 StartZ=0 EndX=1.74589 EndY=-52.1871 EndZ=0
    g14: LineSegment StartX=5.82139 StartY=-60.5461 StartZ=0 EndX=9.9932 EndY=-61.9999 EndZ=0
    g15: ArcOfCircle CenterX=20.4424 CenterY=-28.3787 CenterZ=0 NormalX=0 NormalY=0 NormalZ=1 AngleXU=0 Radius=8.57071 StartAngle=5.18675 EndAngle=6.58262
    g16: ArcOfCircle CenterX=41.8291 CenterY=-56.857 CenterZ=0 NormalX=0 NormalY=0 NormalZ=1 AngleXU=0 Radius=5.82648 StartAngle=3.54306 EndAngle=5.2704
    g17: ArcOfCircle CenterX=40.9895 CenterY=-52.386 CenterZ=0 NormalX=0 NormalY=0 NormalZ=1 AngleXU=0 Radius=10.0638 StartAngle=5.2704 EndAngle=6.38577
    g18: ArcOfCircle CenterX=23.8081 CenterY=-62.4797 CenterZ=0 NormalX=0 NormalY=0 NormalZ=1 AngleXU=0 Radius=12.9588 StartAngle=0.401467 EndAngle=1.17609
    g19: ArcOfCircle CenterX=23.6893 CenterY=-56.2924 CenterZ=0 NormalX=0 NormalY=0 NormalZ=1 AngleXU=0 Radius=7.29288 StartAngle=1.17609 EndAngle=2.89207
    g20: ArcOfCircle CenterX=14.6529 CenterY=-54.7043 CenterZ=0 NormalX=0 NormalY=0 NormalZ=1 AngleXU=0 Radius=1.85585 StartAngle=5.93123 EndAngle=6.03367
    g21: ArcOfCircle CenterX=11.2363 CenterY=-58.4326 CenterZ=0 NormalX=0 NormalY=0 NormalZ=1 AngleXU=0 Radius=3.77769 StartAngle=4.37707 EndAngle=5.93123
    g22: ArcOfCircle CenterX=7.99307 CenterY=-54.3142 CenterZ=0 NormalX=0 NormalY=0 NormalZ=1 AngleXU=0 Radius=6.59939 StartAngle=2.81341 EndAngle=4.37707
    g23: ArcOfCircle CenterX=14.4615 CenterY=-55.9948 CenterZ=0 NormalX=0 NormalY=0 NormalZ=1 AngleXU=0 Radius=13.2643 StartAngle=2.04515 EndAngle=2.81341
    g24: ArcOfCircle CenterX=14.427 CenterY=-31.6225 CenterZ=0 NormalX=0 NormalY=0 NormalZ=1 AngleXU=0 Radius=34.3603 StartAngle=0.102586 EndAngle=0.532404
    g25: ArcOfCircle CenterX=5.20676 CenterY=-28.4747 CenterZ=0 NormalX=0 NormalY=0 NormalZ=1 AngleXU=0 Radius=23.1567 StartAngle=0.299439 EndAngle=0.418209
  constraints (25):
    c: Coincident(g5,g6)
    c: Coincident(g6,g2)
    c: Horizontal(g6)
    c: Tangent(g11,g15) = 1.5708
    c: Tangent(g12,g15) = 1.5708
    c: Tangent(g10,g16) = -1.5708
    c: Tangent(g3,g16) = -1.5708
    c: Tangent(g3,g17) = -1.5708
    c: Tangent(g4,g17) = -1.5708
    c: Tangent(g9,g18) = 1.5708
    c: Tangent(g10,g18) = 1.5708
    c: Tangent(g9,g19) = 1.5708
    c: Tangent(g8,g19) = 1.5708
    c: Tangent(g8,g20) = -1.5708
    c: Tangent(g7,g20) = -1.5708
    c: Tangent(g7,g21) = -1.5708
    c: Tangent(g14,g21) = -1.5708
    c: Tangent(g14,g22) = -1.5708
    c: Tangent(g13,g22) = -1.5708
    c: Tangent(g13,g23) = -1.5708
    c: Tangent(g12,g23) = -1.5708
    c: Tangent(g5,g24) = -1.5708
    c: Tangent(g4,g24) = -1.5708
    c: Tangent(g2,g25) = 1.5708
    c: Tangent(g11,g25) = 1.5708
FEATURE [PartDesign::Pad] Pad349
  BaseFeature = -> Pad348
  Length = 4
  Length2 = 100
  Placement = pos=(0,0,0) rot=(1,0,0;1.5708rad)
  Profile = -> Sketch813
  Type = 0
FEATURE [Sketcher::SketchObject] Sketch815
  MapMode = 5
  Support = -> [XY_Plane028]
  sketch-geometry (10):
    g0: LineSegment StartX=-1.61033 StartY=37.5 StartZ=0 EndX=17.1106 EndY=37.5 EndZ=0
    g1: LineSegment StartX=21.1106 StartY=33.5 StartZ=0 EndX=21.1106 EndY=-33.5 EndZ=0
    g2: LineSegment StartX=17.1106 StartY=-37.5 StartZ=0 EndX=-1.61033 EndY=-37.5 EndZ=0
    g3: LineSegment StartX=-5.61033 StartY=-33.5 StartZ=0 EndX=-5.61033 EndY=33.5 EndZ=0
    g4: ArcOfCircle CenterX=-1.61033 CenterY=33.5 CenterZ=0 NormalX=0 NormalY=0 NormalZ=1 AngleXU=0 Radius=4 StartAngle=1.5708 EndAngle=3.14159
    g5: ArcOfCircle CenterX=17.1106 CenterY=33.5 CenterZ=0 NormalX=0 NormalY=0 NormalZ=1 AngleXU=0 Radius=4 StartAngle=3e-16 EndAngle=1.5708
    g6: ArcOfCircle CenterX=-1.61033 CenterY=-33.5 CenterZ=0 NormalX=0 NormalY=0 NormalZ=1 AngleXU=0 Radius=4 StartAngle=3.14159 EndAngle=4.71239
    g7: ArcOfCircle CenterX=17.1106 CenterY=-33.5 CenterZ=0 NormalX=0 NormalY=0 NormalZ=1 AngleXU=0 Radius=4 StartAngle=4.71239 EndAngle=6.28319
    g8: Circle CenterX=0 CenterY=24.3 CenterZ=0 NormalX=0 NormalY=0 NormalZ=1 AngleXU=0 Radius=1.85
    g9: Circle CenterX=0 CenterY=-31.7 CenterZ=0 NormalX=0 NormalY=0 NormalZ=1 AngleXU=0 Radius=1.85
  constraints (23):
    c: Horizontal(g0)
    c: Horizontal(g2)
    c: Vertical(g1)
    c: Vertical(g3)
    c: Tangent(g3,g4) = 1.5708
    c: Tangent(g0,g4) = 1.5708
    c: Tangent(g0,g5) = 1.5708
    c: Tangent(g1,g5) = 1.5708
    c: Tangent(g3,g6) = 1.5708
    c: Tangent(g2,g6) = 1.5708
    c: Tangent(g2,g7) = 1.5708
    c: Tangent(g1,g7) = 1.5708
    c: Radius(g4) = 4
    c: Equal(g4,g5)
    c: Equal(g5,g7)
    c: DistanceY(g2,g0) = 75
    c: Symmetric(g0,g2,g-1)
    c: PointOnObject(g8,g-2)
    c: PointOnObject(g9,g-2)
    c: Diameter(g8) = 3.7
    c: Equal(g8,g9)
    c: DistanceY(g9,g8) = 56
    c: DistanceY(g8) = 24.3
FEATURE [PartDesign::Pad] Pad351
  Length = 32
  Length2 = 100
  Profile = -> Sketch815
  Type = 0
FEATURE [Sketcher::SketchObject] Sketch816
  AttachmentOffset = pos=(0,0,65) rot=(0,0,1;0rad)
  MapMode = 5
  Placement = pos=(0,0,65) rot=(0,0,1;0rad)
  Support = -> [XY_Plane028]
  sketch-geometry (12):
    g0: LineSegment StartX=-1.94156 StartY=22.2416 StartZ=0 EndX=20.0935 EndY=22.2416 EndZ=0
    g1: LineSegment StartX=30.3381 StartY=22.1834 StartZ=0 EndX=30.3381 EndY=-22.1834 EndZ=0
    g2: LineSegment StartX=20.1466 StartY=-22.2416 StartZ=0 EndX=-1.94156 EndY=-22.2416 EndZ=0
    g3: LineSegment StartX=-1.94156 StartY=-22.2416 StartZ=0 EndX=-1.94156 EndY=22.2416 EndZ=0
    g4: LineSegment StartX=21.1842 StartY=23.3323 StartZ=0 EndX=21.1842 EndY=25.8133 EndZ=0
    g5: LineSegment StartX=21.1842 StartY=25.8133 StartZ=0 EndX=30.3381 EndY=25.8133 EndZ=0
    g6: LineSegment StartX=30.3381 StartY=25.8133 StartZ=0 EndX=30.3381 EndY=22.1834 EndZ=0
    g7: LineSegment StartX=21.145 StartY=-23.24 StartZ=0 EndX=21.145 EndY=-26.6565 EndZ=0
    g8: LineSegment StartX=21.145 StartY=-26.6565 StartZ=0 EndX=30.3381 EndY=-26.6565 EndZ=0
    g9: LineSegment StartX=30.3381 StartY=-26.6565 StartZ=0 EndX=30.3381 EndY=-22.1834 EndZ=0
    g10: ArcOfCircle CenterX=20.0935 CenterY=23.3323 CenterZ=0 NormalX=0 NormalY=0 NormalZ=1 AngleXU=0 Radius=1.09072 StartAngle=4.71239 EndAngle=6.28319
    g11: ArcOfCircle CenterX=20.1466 CenterY=-23.24 CenterZ=0 NormalX=0 NormalY=0 NormalZ=1 AngleXU=0 Radius=0.998398 StartAngle=0 EndAngle=1.5708
  constraints (22):
    c: Coincident(g2,g3)
    c: Coincident(g3,g0)
    c: Horizontal(g0)
    c: Horizontal(g2)
    c: Vertical(g1)
    c: Symmetric(g0,g2,g-1)
    c: Vertical(g4)
    c: Coincident(g4,g5)
    c: Horizontal(g5)
    c: Coincident(g5,g6)
    c: Coincident(g6,g1)
    c: Vertical(g6)
    c: Vertical(g7)
    c: Coincident(g7,g8)
    c: Horizontal(g8)
    c: Coincident(g8,g9)
    c: Coincident(g9,g1)
    c: Vertical(g9)
    c: Tangent(g4,g10) = -1.5708
    c: Tangent(g0,g10) = -1.5708
    c: Tangent(g2,g11) = -1.5708
    c: Tangent(g7,g11) = 1.5708
FEATURE [PartDesign::Pocket] Pocket
  BaseFeature = -> Pad351
  Length = 62
  Length2 = 100
  Profile = -> Sketch816
  Type = 0
FEATURE [Sketcher::SketchObject] Sketch817
  AttachmentOffset = pos=(0,0,4) rot=(0,0,1;0rad)
  MapMode = 5
  Placement = pos=(0,0,4) rot=(0,0,1;0rad)
  Support = -> [XY_Plane028]
  sketch-geometry (10):
    g0: LineSegment StartX=2e-16 StartY=36.1 StartZ=0 EndX=4.75924 EndY=36.1 EndZ=0
    g1: LineSegment StartX=31.1919 StartY=34.2083 StartZ=0 EndX=31.1919 EndY=-34.2083 EndZ=0
    g2: LineSegment StartX=4.75924 StartY=-36.1 StartZ=0 EndX=-9e-16 EndY=-36.1 EndZ=0
    g3: LineSegment StartX=-3.6 StartY=-32.5 StartZ=0 EndX=-3.6 EndY=32.5 EndZ=0
    g4: ArcOfCircle CenterX=0 CenterY=32.5 CenterZ=0 NormalX=0 NormalY=0 NormalZ=1 AngleXU=0 Radius=3.6 StartAngle=1.5708 EndAngle=3.14159
    g5: ArcOfCircle CenterX=0 CenterY=-32.5 CenterZ=0 NormalX=0 NormalY=0 NormalZ=1 AngleXU=0 Radius=3.6 StartAngle=3.14159 EndAngle=4.71239
    g6: LineSegment StartX=4.75924 StartY=36.1 StartZ=0 EndX=10.018 EndY=34.2083 EndZ=0
    g7: LineSegment StartX=10.018 StartY=34.2083 StartZ=0 EndX=31.1919 EndY=34.2083 EndZ=0
    g8: LineSegment StartX=4.75924 StartY=-36.1 StartZ=0 EndX=10.018 EndY=-34.2083 EndZ=0
    g9: LineSegment StartX=10.018 StartY=-34.2083 StartZ=0 EndX=31.1919 EndY=-34.2083 EndZ=0
  constraints (21):
    c: Horizontal(g0)
    c: Horizontal(g2)
    c: Vertical(g1)
    c: Tangent(g3,g4) = 1.5708
    c: Tangent(g0,g4) = 1.5708
    c: Tangent(g3,g5) = 1.5708
    c: Tangent(g2,g5) = 1.5708
    c: Radius(g4) = 3.6
    c: Symmetric(g4,g5,g-1)
    c: DistanceY(g5,g4) = 65
    c: PointOnObject(g5,g-2)
    c: Coincident(g6,g7)
    c: Horizontal(g7)
    c: Coincident(g8,g9)
    c: Horizontal(g9)
    c: Symmetric(g6,g8,g-1)
    c: Coincident(g0,g6)
    c: Coincident(g1,g9)
    c: Coincident(g1,g7)
    c: Coincident(g8,g2)
    c: Symmetric(g0,g2,g-1)
FEATURE [PartDesign::Pocket] Pocket223
  BaseFeature = -> Pocket
  Length = 25
  Length2 = 100
  Profile = -> Sketch817
  Reversed = true
  Type = 0
FEATURE [PartDesign::Body] Body022
  Group = -> [Sketch815,Pad351,Sketch816,Pocket,Sketch817,Pocket223]
  Origin = -> Origin028
  Placement = pos=(218,-96,-111) rot=(0,0,1;3.14159rad)
  Tip = -> Pocket223
FEATURE [Sketcher::SketchObject] Sketch821
  MapMode = 5
  Placement = pos=(0,0,0) rot=(1,0,0;1.5708rad)
  Support = -> [XZ_Plane]
  sketch-geometry (22):
    g0: LineSegment StartX=22.1563 StartY=112.186 StartZ=0 EndX=27.5687 EndY=112.186 EndZ=0
    g1: LineSegment StartX=27.5687 StartY=112.186 StartZ=0 EndX=27.5687 EndY=94.657 EndZ=0
    g2: LineSegment StartX=27.5687 StartY=94.657 StartZ=0 EndX=30.5256 EndY=85.9063 EndZ=0
    g3: LineSegment StartX=30.5256 StartY=85.9063 StartZ=0 EndX=35.0126 EndY=65.899 EndZ=0
    g4: LineSegment StartX=35.0126 StartY=65.899 StartZ=0 EndX=42.2181 EndY=54.7235 EndZ=0
    g5: LineSegment StartX=42.2181 StartY=54.7235 StartZ=0 EndX=56.8396 EndY=54.7743 EndZ=0
    g6: LineSegment StartX=56.8396 StartY=54.7743 StartZ=0 EndX=59.2312 EndY=41.9171 EndZ=0
    g7: LineSegment StartX=59.2312 StartY=41.9171 StartZ=0 EndX=58.6538 EndY=37.8967 EndZ=0
    g8: LineSegment StartX=58.6538 StartY=37.8967 StartZ=0 EndX=44.2789 EndY=37.8967 EndZ=0
    g9: LineSegment StartX=44.2789 StartY=37.8967 StartZ=0 EndX=41.3697 EndY=26.9188 EndZ=0
    g10: LineSegment StartX=41.3697 StartY=26.9188 StartZ=0 EndX=52.8065 EndY=14.9529 EndZ=0
    g11: LineSegment StartX=52.8065 StartY=14.9529 StartZ=0 EndX=49.0434 EndY=10.9243 EndZ=0
    g12: LineSegment StartX=49.0434 StartY=10.9243 StartZ=0 EndX=37.2945 EndY=24.9476 EndZ=0
    g13: LineSegment StartX=37.2945 StartY=24.9476 StartZ=0 EndX=40.6511 EndY=40.3013 EndZ=0
    g14: LineSegment StartX=40.6511 StartY=40.3013 StartZ=0 EndX=36.4766 EndY=54.3174 EndZ=0
    g15: LineSegment StartX=36.4766 StartY=54.3174 StartZ=0 EndX=28.9877 EndY=65.7559 EndZ=0
    g16: LineSegment StartX=28.9877 StartY=65.7559 StartZ=0 EndX=22.1563 EndY=91.9357 EndZ=0
    g17: LineSegment StartX=22.1563 StartY=91.9357 StartZ=0 EndX=22.1563 EndY=112.186 EndZ=0
    g18: LineSegment StartX=43.7074 StartY=49.7667 StartZ=0 EndX=55.0871 EndY=49.7667 EndZ=0
    g19: LineSegment StartX=55.0871 StartY=49.7667 StartZ=0 EndX=55.0871 EndY=42.3366 EndZ=0
    g20: LineSegment StartX=55.0871 StartY=42.3366 StartZ=0 EndX=43.7074 EndY=42.3366 EndZ=0
    g21: LineSegment StartX=43.7074 StartY=42.3366 StartZ=0 EndX=43.7074 EndY=49.7667 EndZ=0
  constraints (30):
    c: Horizontal(g0)
    c: Coincident(g0,g1)
    c: Vertical(g1)
    c: Coincident(g1,g2)
    c: Coincident(g2,g3)
    c: Coincident(g3,g4)
    c: Coincident(g4,g5)
    c: Coincident(g5,g6)
    c: Coincident(g6,g7)
    c: Coincident(g7,g8)
    c: Horizontal(g8)
    c: Coincident(g8,g9)
    c: Coincident(g9,g10)
    c: Coincident(g10,g11)
    c: Coincident(g11,g12)
    c: Coincident(g12,g13)
    c: Coincident(g13,g14)
    c: Coincident(g14,g15)
    c: Coincident(g15,g16)
    c: Coincident(g16,g17)
    c: Coincident(g17,g0)
    c: Vertical(g17)
    c: Coincident(g18,g19)
    c: Coincident(g19,g20)
    c: Coincident(g20,g21)
    c: Coincident(g21,g18)
    c: Horizontal(g18)
    c: Horizontal(g20)
    c: Vertical(g19)
    c: Vertical(g21)
FEATURE [PartDesign::Pad] Pad355
  BaseFeature = -> Pad349
  Length = 10
  Length2 = 100
  Placement = pos=(0,0,0) rot=(1,0,0;1.5708rad)
  Profile = -> Sketch821
  Type = 0
FEATURE [Sketcher::SketchObject] Sketch830
  MapMode = 5
  Placement = pos=(0,0,0) rot=(1,0,0;1.5708rad)
  Support = -> [XZ_Plane030]
  sketch-geometry (15):
    g0: LineSegment [constr] StartX=-40 StartY=24.4988 StartZ=0 EndX=-40 EndY=-122.387 EndZ=0
    g1: LineSegment StartX=-1.47853 StartY=-110.025 StartZ=0 EndX=137.371 EndY=-110.025 EndZ=0
    g2: LineSegment StartX=0.022068 StartY=4.37461 StartZ=0 EndX=1.50821 EndY=4.37461 EndZ=0
    g3: ArcOfCircle CenterX=0.0220675 CenterY=-35.105 CenterZ=0 NormalX=0 NormalY=0 NormalZ=1 AngleXU=0 Radius=39.4796 StartAngle=1.5708 EndAngle=3.0266
    g4: ArcOfCircle CenterX=171.277 CenterY=-54.8849 CenterZ=0 NormalX=0 NormalY=0 NormalZ=1 AngleXU=0 Radius=211.873 StartAngle=3.0266 EndAngle=3.23877
    g5: ArcOfCircle CenterX=-1.47853 CenterY=-71.7266 CenterZ=0 NormalX=0 NormalY=0 NormalZ=1 AngleXU=0 Radius=38.2986 StartAngle=3.23877 EndAngle=4.71239
    g6: ArcOfCircle CenterX=1.50821 CenterY=7.27475 CenterZ=0 NormalX=0 NormalY=0 NormalZ=1 AngleXU=0 Radius=2.90014 StartAngle=4.71239 EndAngle=5.35213
    g7: ArcOfCircle CenterX=1.50821 CenterY=7.27475 CenterZ=0 NormalX=0 NormalY=0 NormalZ=1 AngleXU=0 Radius=3.7451 StartAngle=4.72214 EndAngle=5.36454
    g8: LineSegment StartX=1.54474 StartY=3.52982 StartZ=0 EndX=8.062e-13 EndY=1.37497 EndZ=0
    g9: ArcOfCircle CenterX=0.0220675 CenterY=-35.105 CenterZ=0 NormalX=0 NormalY=0 NormalZ=1 AngleXU=0 Radius=36.48 StartAngle=1.5714 EndAngle=3.01961
    g10: ArcOfCircle CenterX=171.277 CenterY=-54.8849 CenterZ=0 NormalX=0 NormalY=0 NormalZ=1 AngleXU=0 Radius=208.873 StartAngle=3.02538 EndAngle=3.23966
    g11: ArcOfCircle CenterX=-1.47853 CenterY=-71.7266 CenterZ=0 NormalX=0 NormalY=0 NormalZ=1 AngleXU=0 Radius=35.2986 StartAngle=3.24402 EndAngle=4.71372
    g12: LineSegment StartX=-1.43157 StartY=-107.025 StartZ=0 EndX=137.371 EndY=-107.025 EndZ=0
    g13: LineSegment StartX=137.371 StartY=-107.025 StartZ=0 EndX=137.371 EndY=-110.025 EndZ=0
    g14: LineSegment StartX=3.23956 StartY=4.94812 StartZ=0 EndX=3.78111 EndY=4.29822 EndZ=0
  constraints (36):
    c: Vertical(g0)
    c: DistanceX(g0,g-1) = 40
    c: Horizontal(g1)
    c: DistanceX(g1) = -1.47853
    c: DistanceY(g1) = -110.025
    c: Coincident(g3,g2)
    c: Horizontal(g2)
    c: Tangent(g2,g3)
    c: DistanceX(g2) = 0.022068
    c: DistanceY(g2) = 4.37461
    c: Coincident(g4,g3)
    c: Tangent(g3,g4)
    c: Coincident(g5,g4)
    c: Coincident(g5,g1)
    c: Tangent(g5,g4)
    c: Tangent(g5,g1)
    c: Coincident(g6,g2)
    c: Tangent(g6,g2)
    c: DistanceX(g2) = 1.50821
    c: Coincident(g7,g6)
    c: Coincident(g8,g7)
    c: PointOnObject(g8,g-2)
    c: Coincident(g9,g3)
    c: Coincident(g9,g8)
    c: Coincident(g10,g4)
    c: Coincident(g10,g9)
    c: Coincident(g11,g5)
    c: Coincident(g11,g10)
    c: Coincident(g12,g11)
    c: Horizontal(g12)
    c: Coincident(g13,g12)
    c: Coincident(g13,g1)
    c: Vertical(g13)
    c: DistanceY(g13,g13) = 3
    c: Coincident(g14,g6)
    c: Coincident(g14,g7)
FEATURE [PartDesign::Pad] Pad356
  Length = 12.5
  Length2 = 100
  Placement = pos=(0,0,0) rot=(1,0,0;1.5708rad)
  Profile = -> Sketch830
  Type = 0
FEATURE [Sketcher::SketchObject] Sketch831
  MapMode = 5
  Placement = pos=(0,0,0) rot=(1,0,0;1.5708rad)
  Support = -> [XZ_Plane030]
  sketch-geometry (45):
    g0: LineSegment StartX=-11.207 StartY=4.99592 StartZ=0 EndX=2.08106 EndY=7.17118 EndZ=0
    g1: LineSegment StartX=2.08106 StartY=7.17118 StartZ=0 EndX=3.88495 EndY=3.34693 EndZ=0
    g2: LineSegment StartX=3.88495 StartY=3.34693 StartZ=0 EndX=-3.07198 EndY=-0.758803 EndZ=0
    g3: LineSegment StartX=-3.07198 StartY=-0.758803 StartZ=0 EndX=-10.9561 EndY=-4.60959 EndZ=0
    g4: LineSegment StartX=-10.9561 StartY=-4.60959 StartZ=0 EndX=-19.8966 EndY=-10.7507 EndZ=0
    g5: LineSegment StartX=-19.8966 StartY=-10.7507 StartZ=0 EndX=-25.5171 EndY=-17.1741 EndZ=0
    g6: LineSegment StartX=-25.5171 StartY=-17.1741 StartZ=0 EndX=-31.1745 EndY=-28.9416 EndZ=0
    g7: LineSegment StartX=-31.1745 StartY=-28.9416 StartZ=0 EndX=-31.1745 EndY=-40.8451 EndZ=0
    g8: LineSegment StartX=-30.8325 StartY=-64.5615 StartZ=0 EndX=-30.2076 EndY=-73.1621 EndZ=0
    g9: LineSegment StartX=-30.2076 StartY=-73.1621 StartZ=0 EndX=-27.1543 EndY=-83.9449 EndZ=0
    g10: LineSegment StartX=-27.1543 StartY=-83.9449 StartZ=0 EndX=-18.9644 EndY=-93.4998 EndZ=0
    g11: LineSegment StartX=-18.9644 StartY=-93.4998 StartZ=0 EndX=-9.16868 EndY=-98.5582 EndZ=0
    g12: LineSegment StartX=-9.16868 StartY=-98.5582 StartZ=0 EndX=-2.33134 EndY=-98.5582 EndZ=0
    g13: LineSegment StartX=-2.33134 StartY=-98.5582 StartZ=0 EndX=137.626 EndY=-98.5582 EndZ=0
    g14: LineSegment StartX=137.626 StartY=-98.5582 StartZ=0 EndX=137.148 EndY=-109.564 EndZ=0
    g15: LineSegment StartX=137.148 StartY=-109.564 StartZ=0 EndX=2.74599 EndY=-109.564 EndZ=0
    g16: LineSegment StartX=2.74599 StartY=-109.564 StartZ=0 EndX=-3.35627 EndY=-109.564 EndZ=0
    g17: LineSegment StartX=-3.35627 StartY=-109.564 StartZ=0 EndX=-8.52775 EndY=-108.904 EndZ=0
    g18: LineSegment StartX=-8.52775 StartY=-108.904 StartZ=0 EndX=-14.661 EndY=-106.811 EndZ=0
    g19: LineSegment StartX=-14.661 StartY=-106.811 StartZ=0 EndX=-18.7378 EndY=-105.296 EndZ=0
    g20: LineSegment StartX=-18.7378 StartY=-105.296 StartZ=0 EndX=-23.0311 EndY=-102.843 EndZ=0
    g21: LineSegment StartX=-23.0311 StartY=-102.843 StartZ=0 EndX=-25.9664 EndY=-100.308 EndZ=0
    g22: LineSegment StartX=-25.9664 StartY=-100.308 StartZ=0 EndX=-29.7185 EndY=-96.7728 EndZ=0
    g23: LineSegment StartX=-29.7185 StartY=-96.7728 StartZ=0 EndX=-33.8674 EndY=-91.1085 EndZ=0
    g24: LineSegment StartX=-33.8674 StartY=-91.1085 StartZ=0 EndX=-35.4091 EndY=-87.7046 EndZ=0
    g25: LineSegment StartX=-35.4091 StartY=-87.7046 StartZ=0 EndX=-37.577 EndY=-82.887 EndZ=0
    g26: LineSegment StartX=-37.577 StartY=-82.887 StartZ=0 EndX=-39.0223 EndY=-76.1424 EndZ=0
    g27: LineSegment StartX=-39.0223 StartY=-76.1424 StartZ=0 EndX=-39.504 EndY=-68.9161 EndZ=0
    g28: LineSegment StartX=-39.504 StartY=-68.9161 StartZ=0 EndX=-39.7958 EndY=-62.945 EndZ=0
    g29: LineSegment StartX=-39.7958 StartY=-62.945 StartZ=0 EndX=-39.7958 EndY=-54.1183 EndZ=0
    g30: LineSegment StartX=-39.7958 StartY=-54.1183 StartZ=0 EndX=-39.7958 EndY=-44.6795 EndZ=0
    g31: LineSegment StartX=-39.7958 StartY=-44.6795 StartZ=0 EndX=-38.559 EndY=-32.3543 EndZ=0
    g32: LineSegment StartX=-38.559 StartY=-32.3543 StartZ=0 EndX=-38.3955 EndY=-29.4237 EndZ=0
    g33: LineSegment StartX=-38.3955 StartY=-29.4237 StartZ=0 EndX=-36.6194 EndY=-22.3192 EndZ=0
    g34: LineSegment StartX=-36.6194 StartY=-22.3192 StartZ=0 EndX=-33.1748 EndY=-14.7303 EndZ=0
    g35: LineSegment StartX=-33.1748 StartY=-14.7303 StartZ=0 EndX=-28.8067 EndY=-8.89013 EndZ=0
    g36: LineSegment StartX=-28.8067 StartY=-8.89013 StartZ=0 EndX=-22.7249 EndY=-3.6694 EndZ=0
    g37: LineSegment StartX=-22.7249 StartY=-3.6694 StartZ=0 EndX=-15.8357 EndY=1.92807 EndZ=0
    g38: LineSegment StartX=-15.8357 StartY=1.92807 StartZ=0 EndX=-11.207 EndY=4.99592 EndZ=0
    g39: LineSegment StartX=-26.0329 StartY=-52.1456 StartZ=0 EndX=-0.596695 EndY=-52.1456 EndZ=0
    g40: LineSegment StartX=-0.596695 StartY=-52.1456 StartZ=0 EndX=-0.596695 EndY=-59.8538 EndZ=0
    g41: LineSegment StartX=-0.596695 StartY=-59.8538 StartZ=0 EndX=-26.4543 EndY=-59.8538 EndZ=0
    g42: LineSegment StartX=-31.1745 StartY=-40.8451 StartZ=0 EndX=-31.1745 EndY=-47.0041 EndZ=0
    g43: ArcOfCircle CenterX=-26.0329 CenterY=-47.0041 CenterZ=0 NormalX=0 NormalY=0 NormalZ=1 AngleXU=0 Radius=5.14156 StartAngle=3.14159 EndAngle=4.71239
    g44: ArcOfCircle CenterX=-26.4543 CenterY=-64.2435 CenterZ=0 NormalX=0 NormalY=0 NormalZ=1 AngleXU=0 Radius=4.38969 StartAngle=1.5708 EndAngle=3.21412
  constraints (56):
    c: Coincident(g0,g1)
    c: Coincident(g1,g2)
    c: Coincident(g2,g3)
    c: Coincident(g3,g4)
    c: Coincident(g4,g5)
    c: Coincident(g5,g6)
    c: Coincident(g6,g7)
    c: Vertical(g7)
    c: Coincident(g8,g9)
    c: Coincident(g9,g10)
    c: Coincident(g10,g11)
    c: Coincident(g11,g12)
    c: Horizontal(g12)
    c: Coincident(g12,g13)
    c: Horizontal(g13)
    c: Coincident(g13,g14)
    c: Coincident(g14,g15)
    c: Horizontal(g15)
    c: Coincident(g15,g16)
    c: Horizontal(g16)
    c: Coincident(g16,g17)
    c: Coincident(g17,g18)
    c: Coincident(g18,g19)
    c: Coincident(g19,g20)
    c: Coincident(g20,g21)
    c: Coincident(g21,g22)
    c: Coincident(g22,g23)
    c: Coincident(g23,g24)
    c: Coincident(g24,g25)
    c: Coincident(g25,g26)
    c: Coincident(g26,g27)
    c: Coincident(g27,g28)
    c: Coincident(g28,g29)
    c: Vertical(g29)
    c: Coincident(g29,g30)
    c: Vertical(g30)
    c: Coincident(g30,g31)
    c: Coincident(g31,g32)
    c: Coincident(g32,g33)
    c: Coincident(g33,g34)
    c: Coincident(g34,g35)
    c: Coincident(g35,g36)
    c: Coincident(g36,g37)
    c: Coincident(g37,g38)
    c: Coincident(g38,g0)
    c: Horizontal(g39)
    c: Coincident(g39,g40)
    c: Vertical(g40)
    c: Coincident(g40,g41)
    c: Horizontal(g41)
    c: Coincident(g42,g7)
    c: Vertical(g42)
    c: Tangent(g42,g43) = -1.5708
    c: Tangent(g39,g43) = -1.5708
    c: Tangent(g8,g44) = -1.5708
    c: Tangent(g41,g44) = -1.5708
FEATURE [PartDesign::Pad] Pad357
  BaseFeature = -> Pad356
  Length = 1.5
  Length2 = 100
  Placement = pos=(0,0,0) rot=(1,0,0;1.5708rad)
  Profile = -> Sketch831
  Type = 0
FEATURE [Sketcher::SketchObject] Sketch834
  AttachmentOffset = pos=(0,0,14) rot=(0,0,1;0rad)
  MapMode = 5
  Placement = pos=(0,-14,-3.1e-15) rot=(1,0,0;1.5708rad)
  Support = -> [XZ_Plane031]
  sketch-geometry (27):
    g0: LineSegment StartX=3.88495 StartY=3.34693 StartZ=0 EndX=-3.07198 EndY=-0.758803 EndZ=0
    g1: LineSegment StartX=-3.07198 StartY=-0.758803 StartZ=0 EndX=-10.9561 EndY=-4.60959 EndZ=0
    g2: LineSegment StartX=-10.9561 StartY=-4.60959 StartZ=0 EndX=-19.8966 EndY=-10.7507 EndZ=0
    g3: LineSegment StartX=-19.8966 StartY=-10.7507 StartZ=0 EndX=-25.5171 EndY=-17.1741 EndZ=0
    g4: LineSegment StartX=-25.5171 StartY=-17.1741 StartZ=0 EndX=-31.1745 EndY=-28.9416 EndZ=0
    g5: LineSegment StartX=-31.1745 StartY=-28.9416 StartZ=0 EndX=-31.1745 EndY=-40.8451 EndZ=0
    g6: LineSegment StartX=-30.8325 StartY=-64.5615 StartZ=0 EndX=-30.2076 EndY=-73.1621 EndZ=0
    g7: LineSegment StartX=-30.2076 StartY=-73.1621 StartZ=0 EndX=-27.1543 EndY=-83.9449 EndZ=0
    g8: LineSegment StartX=-27.1543 StartY=-83.9449 StartZ=0 EndX=-18.9644 EndY=-93.4998 EndZ=0
    g9: LineSegment StartX=-18.9644 StartY=-93.4998 StartZ=0 EndX=-9.16868 EndY=-98.5632 EndZ=0
    g10: LineSegment StartX=-9.16868 StartY=-98.5632 StartZ=0 EndX=-2.33134 EndY=-98.5632 EndZ=0
    g11: LineSegment StartX=-2.33134 StartY=-98.5632 StartZ=0 EndX=137.371 EndY=-98.5632 EndZ=0
    g12: LineSegment StartX=-26.0329 StartY=-52.1456 StartZ=0 EndX=-0.596695 EndY=-52.1456 EndZ=0
    g13: LineSegment StartX=-0.596695 StartY=-52.1456 StartZ=0 EndX=-0.596695 EndY=-59.8538 EndZ=0
    g14: LineSegment StartX=-0.596695 StartY=-59.8538 StartZ=0 EndX=-26.4543 EndY=-59.8538 EndZ=0
    g15: LineSegment StartX=-31.1745 StartY=-40.8451 StartZ=0 EndX=-31.1745 EndY=-47.0041 EndZ=0
    g16: ArcOfCircle CenterX=-26.0329 CenterY=-47.0041 CenterZ=0 NormalX=0 NormalY=0 NormalZ=1 AngleXU=0 Radius=5.14156 StartAngle=3.14159 EndAngle=4.71239
    g17: ArcOfCircle CenterX=-26.4543 CenterY=-64.2435 CenterZ=0 NormalX=0 NormalY=0 NormalZ=1 AngleXU=0 Radius=4.38969 StartAngle=1.5708 EndAngle=3.21412
    g18: LineSegment [constr] StartX=-40 StartY=24.4988 StartZ=0 EndX=-40 EndY=-122.387 EndZ=0
    g19: LineSegment StartX=-1.47853 StartY=-110.025 StartZ=0 EndX=137.371 EndY=-110.025 EndZ=0
    g20: LineSegment StartX=0.022068 StartY=4.37461 StartZ=0 EndX=1.50821 EndY=4.37461 EndZ=0
    g21: ArcOfCircle CenterX=0.0220678 CenterY=-35.0467 CenterZ=0 NormalX=0 NormalY=0 NormalZ=1 AngleXU=0 Radius=39.4213 StartAngle=1.5708 EndAngle=3.02493
    g22: ArcOfCircle CenterX=171.294 CenterY=-55.1183 CenterZ=0 NormalX=0 NormalY=0 NormalZ=1 AngleXU=0 Radius=211.865 StartAngle=3.02493 EndAngle=3.23744
    g23: ArcOfCircle CenterX=-1.47853 CenterY=-71.729 CenterZ=0 NormalX=0 NormalY=0 NormalZ=1 AngleXU=0 Radius=38.2962 StartAngle=3.23744 EndAngle=4.71239
    g24: ArcOfCircle CenterX=1.50821 CenterY=6.84639 CenterZ=0 NormalX=0 NormalY=0 NormalZ=1 AngleXU=0 Radius=2.47178 StartAngle=4.71239 EndAngle=5.4414
    g25: LineSegment StartX=137.371 StartY=-98.5632 StartZ=0 EndX=137.371 EndY=-110.025 EndZ=0
    g26: LineSegment StartX=3.15474 StartY=5.00285 StartZ=0 EndX=3.88495 EndY=3.34693 EndZ=0
  constraints (48):
    c: Coincident(g0,g1)
    c: Coincident(g1,g2)
    c: Coincident(g2,g3)
    c: Coincident(g3,g4)
    c: Coincident(g4,g5)
    c: Vertical(g5)
    c: Coincident(g6,g7)
    c: Coincident(g7,g8)
    c: Coincident(g8,g9)
    c: Coincident(g9,g10)
    c: Horizontal(g10)
    c: Coincident(g10,g11)
    c: Horizontal(g11)
    c: Horizontal(g12)
    c: Coincident(g12,g13)
    c: Vertical(g13)
    c: Coincident(g13,g14)
    c: Horizontal(g14)
    c: Coincident(g15,g5)
    c: Vertical(g15)
    c: Tangent(g15,g16) = -1.5708
    c: Tangent(g12,g16) = -1.5708
    c: Tangent(g6,g17) = -1.5708
    c: Tangent(g14,g17) = -1.5708
    c: Vertical(g18)
    c: DistanceX(g18,g-1) = 40
    c: Horizontal(g19)
    c: DistanceX(g19) = -1.47853
    c: DistanceY(g19) = -110.025
    c: Coincident(g21,g20)
    c: Horizontal(g20)
    c: Tangent(g20,g21)
    c: DistanceX(g20) = 0.022068
    c: DistanceY(g20) = 4.37461
    c: Coincident(g22,g21)
    c: Tangent(g21,g22)
    c: Coincident(g23,g22)
    c: Coincident(g23,g19)
    c: Tangent(g23,g22)
    c: Tangent(g23,g19)
    c: Coincident(g24,g20)
    c: Tangent(g24,g20)
    c: DistanceX(g20) = 1.50821
    c: Coincident(g25,g11)
    c: Coincident(g25,g19)
    c: Vertical(g25)
    c: Coincident(g26,g24)
    c: Coincident(g26,g0)
FEATURE [PartDesign::Pad] Pad358
  Length = 1.5
  Length2 = 100
  Placement = pos=(0,0,0) rot=(1,0,0;1.5708rad)
  Profile = -> Sketch834
  Reversed = true
  Type = 0
FEATURE [PartDesign::Body] Body025
  Group = -> [Sketch834,Pad358]
  Origin = -> Origin031
  Placement = pos=(88,-111,4) rot=(0,0,1;0rad)
  Tip = -> Pad358
FEATURE [Sketcher::SketchObject] Sketch835
  AttachmentOffset = pos=(0,0,1.5) rot=(0,0,1;0rad)
  MapMode = 5
  Placement = pos=(0,-1.5,-3e-16) rot=(1,0,0;1.5708rad)
  Support = -> [XZ_Plane030]
  sketch-geometry (45):
    g0: LineSegment StartX=-10.7972 StartY=-4.39096 StartZ=0 EndX=-5.61734 EndY=-1.86668 EndZ=0
    g1: LineSegment StartX=-5.61734 StartY=-1.86668 StartZ=0 EndX=-9.44766 EndY=-2.50994 EndZ=0
    g2: LineSegment StartX=-9.44766 StartY=-2.50994 StartZ=0 EndX=-10.7972 EndY=-4.39096 EndZ=0
    g3: LineSegment StartX=-19.4023 StartY=-10.3566 StartZ=0 EndX=-15.4124 EndY=-7.53908 EndZ=0
    g4: LineSegment StartX=-15.4124 StartY=-7.53908 StartZ=0 EndX=-18.8042 EndY=-8.03614 EndZ=0
    g5: LineSegment StartX=-18.8042 StartY=-8.03614 StartZ=0 EndX=-19.4023 EndY=-10.3566 EndZ=0
    g6: LineSegment StartX=-25.5409 StartY=-17.1853 StartZ=0 EndX=-22.0807 EndY=-13.1617 EndZ=0
    g7: LineSegment StartX=-22.0807 StartY=-13.1617 StartZ=0 EndX=-25.7356 EndY=-14.5067 EndZ=0
    g8: LineSegment StartX=-25.7356 StartY=-14.5067 StartZ=0 EndX=-25.5409 EndY=-17.1853 EndZ=0
    g9: LineSegment StartX=-28.7497 StartY=-23.7597 StartZ=0 EndX=-31.1327 EndY=-28.7661 EndZ=0
    g10: LineSegment StartX=-31.1327 StartY=-28.7661 StartZ=0 EndX=-31.1766 EndY=-25.3094 EndZ=0
    g11: LineSegment StartX=-31.1766 StartY=-25.3094 StartZ=0 EndX=-28.7497 EndY=-23.7597 EndZ=0
    g12: LineSegment StartX=-31.2627 StartY=-39.8223 StartZ=0 EndX=-31.2627 EndY=-45.6292 EndZ=0
    g13: LineSegment StartX=-31.2627 StartY=-45.6292 StartZ=0 EndX=-32.6954 EndY=-42.6 EndZ=0
    g14: LineSegment StartX=-32.6954 StartY=-42.6 StartZ=0 EndX=-31.2627 EndY=-39.8223 EndZ=0
    g15: LineSegment StartX=-2.73346 StartY=-52.178 StartZ=0 EndX=-0.602387 EndY=-52.178 EndZ=0
    g16: LineSegment StartX=-0.602387 StartY=-52.178 StartZ=0 EndX=-0.602387 EndY=-59.7974 EndZ=0
    g17: LineSegment StartX=-0.602387 StartY=-59.7974 StartZ=0 EndX=-2.73346 EndY=-59.7974 EndZ=0
    g18: LineSegment StartX=-2.73346 StartY=-59.7974 StartZ=0 EndX=-2.73346 EndY=-52.178 EndZ=0
    g19: LineSegment StartX=-19.9819 StartY=-52.2195 StartZ=0 EndX=-16.8346 EndY=-52.2195 EndZ=0
    g20: LineSegment StartX=-16.8346 StartY=-52.2195 StartZ=0 EndX=-16.8346 EndY=-59.7363 EndZ=0
    g21: LineSegment StartX=-16.8346 StartY=-59.7363 StartZ=0 EndX=-19.9819 EndY=-59.7363 EndZ=0
    g22: LineSegment StartX=-19.9819 StartY=-59.7363 StartZ=0 EndX=-19.9819 EndY=-52.2195 EndZ=0
    g23: LineSegment StartX=-30.8834 StartY=-63.9775 StartZ=0 EndX=-30.474 EndY=-69.9716 EndZ=0
    g24: LineSegment StartX=-30.474 StartY=-69.9716 StartZ=0 EndX=-32.4038 EndY=-67.4278 EndZ=0
    g25: LineSegment StartX=-32.4038 StartY=-67.4278 StartZ=0 EndX=-30.8834 EndY=-63.9775 EndZ=0
    g26: LineSegment StartX=-29.1781 StartY=-76.971 StartZ=0 EndX=-27.7837 EndY=-82.0307 EndZ=0
    g27: LineSegment StartX=-27.7837 StartY=-82.0307 StartZ=0 EndX=-29.8048 EndY=-80.1963 EndZ=0
    g28: LineSegment StartX=-29.8048 StartY=-80.1963 StartZ=0 EndX=-29.1781 EndY=-76.971 EndZ=0
    g29: LineSegment StartX=-23.0497 StartY=-88.873 StartZ=0 EndX=-19.2517 EndY=-93.2154 EndZ=0
    g30: LineSegment StartX=-19.2517 StartY=-93.2154 StartZ=0 EndX=-22.8261 EndY=-92.2158 EndZ=0
    g31: LineSegment StartX=-22.8261 StartY=-92.2158 StartZ=0 EndX=-23.0497 EndY=-88.873 EndZ=0
    g32: LineSegment StartX=-14.3347 StartY=-95.8938 StartZ=0 EndX=-9.42002 EndY=-98.5824 EndZ=0
    g33: LineSegment StartX=-9.42002 StartY=-98.5824 StartZ=0 EndX=-13.3405 EndY=-98.3206 EndZ=0
    g34: LineSegment StartX=-13.3405 StartY=-98.3206 StartZ=0 EndX=-14.3347 EndY=-95.8938 EndZ=0
    g35: LineSegment StartX=33.0742 StartY=-98.6339 StartZ=0 EndX=41.6167 EndY=-98.6339 EndZ=0
    g36: LineSegment StartX=41.6167 StartY=-98.6339 StartZ=0 EndX=37.2406 EndY=-100.138 EndZ=0
    g37: LineSegment StartX=37.2406 StartY=-100.138 StartZ=0 EndX=33.0742 EndY=-98.6339 EndZ=0
    g38: LineSegment StartX=71.901 StartY=-98.7225 StartZ=0 EndX=81.0251 EndY=-98.7225 EndZ=0
    g39: LineSegment StartX=81.0251 StartY=-98.7225 StartZ=0 EndX=76.5123 EndY=-100.363 EndZ=0
    g40: LineSegment StartX=76.5123 StartY=-100.363 StartZ=0 EndX=71.901 EndY=-98.7225 EndZ=0
    g41: LineSegment StartX=135.083 StartY=-98.657 StartZ=0 EndX=135.206 EndY=-100.521 EndZ=0
    g42: LineSegment StartX=135.206 StartY=-100.521 StartZ=0 EndX=137.438 EndY=-100.255 EndZ=0
    g43: LineSegment StartX=137.438 StartY=-100.255 StartZ=0 EndX=137.541 EndY=-98.657 EndZ=0
    g44: LineSegment StartX=137.541 StartY=-98.657 StartZ=0 EndX=135.083 EndY=-98.657 EndZ=0
  constraints (56):
    c: Coincident(g0,g1)
    c: Coincident(g1,g2)
    c: Coincident(g2,g0)
    c: Coincident(g3,g4)
    c: Coincident(g4,g5)
    c: Coincident(g5,g3)
    c: Coincident(g6,g7)
    c: Coincident(g7,g8)
    c: Coincident(g8,g6)
    c: Coincident(g9,g10)
    c: Coincident(g10,g11)
    c: Coincident(g11,g9)
    c: Vertical(g12)
    c: Coincident(g12,g13)
    c: Coincident(g13,g14)
    c: Coincident(g14,g12)
    c: Coincident(g15,g16)
    c: Coincident(g16,g17)
    c: Coincident(g17,g18)
    c: Coincident(g18,g15)
    c: Horizontal(g15)
    c: Horizontal(g17)
    c: Vertical(g16)
    c: Vertical(g18)
    c: Coincident(g19,g20)
    c: Coincident(g20,g21)
    c: Coincident(g21,g22)
    c: Coincident(g22,g19)
    c: Horizontal(g19)
    c: Horizontal(g21)
    c: Vertical(g20)
    c: Vertical(g22)
    c: Coincident(g23,g24)
    c: Coincident(g24,g25)
    c: Coincident(g25,g23)
    c: Coincident(g26,g27)
    c: Coincident(g27,g28)
    c: Coincident(g28,g26)
    c: Coincident(g29,g30)
    c: Coincident(g30,g31)
    c: Coincident(g31,g29)
    c: Coincident(g32,g33)
    c: Coincident(g33,g34)
    c: Coincident(g34,g32)
    c: Horizontal(g35)
    c: Coincident(g35,g36)
    c: Coincident(g36,g37)
    c: Coincident(g37,g35)
    c: Horizontal(g38)
    c: Coincident(g38,g39)
    c: Coincident(g39,g40)
    c: Coincident(g40,g38)
    c: Coincident(g41,g42)
    c: Coincident(g42,g43)
    c: Coincident(g43,g44)
    c: Coincident(g44,g41)
FEATURE [PartDesign::Pad] Pad359
  BaseFeature = -> Pad357
  Length = 11
  Length2 = 100
  Placement = pos=(0,0,0) rot=(1,0,0;1.5708rad)
  Profile = -> Sketch835
  Type = 0
FEATURE [PartDesign::Body] Body024
  Group = -> [Sketch830,Pad356,Sketch831,Pad357,Sketch835,Pad359]
  Origin = -> Origin030
  Placement = pos=(88,-111,4) rot=(0,0,1;0rad)
  Tip = -> Pad359
FEATURE [Sketcher::SketchObject] Sketch836
  MapMode = 5
  Support = -> [XY_Plane032]
  sketch-geometry (8):
    g0: ArcOfCircle CenterX=0 CenterY=0 CenterZ=0 NormalX=0 NormalY=0 NormalZ=1 AngleXU=0 Radius=9.25 StartAngle=4.96402 EndAngle=10.7439
    g1: ArcOfCircle CenterX=0 CenterY=0 CenterZ=0 NormalX=0 NormalY=0 NormalZ=1 AngleXU=0 Radius=16.4419 StartAngle=1.60475 EndAngle=5.58385
    g2: ArcOfCircle CenterX=0 CenterY=-8.00171 CenterZ=0 NormalX=0 NormalY=0 NormalZ=1 AngleXU=0 Radius=2.494 StartAngle=3.53541 EndAngle=5.88937
    g3: LineSegment StartX=12.5825 StartY=-10.5837 StartZ=0 EndX=20 EndY=-1.76543 EndZ=0
    g4: LineSegment StartX=20 StartY=-1.76543 StartZ=0 EndX=20 EndY=11 EndZ=0
    g5: LineSegment StartX=6.52776 StartY=16.4324 StartZ=0 EndX=-0.558167 EndY=16.4324 EndZ=0
    g6: LineSegment StartX=6.52776 StartY=16.4324 StartZ=0 EndX=8 EndY=11 EndZ=0
    g7: LineSegment StartX=8 StartY=11 StartZ=0 EndX=20 EndY=11 EndZ=0
  constraints (16):
    c: PointOnObject(g0,g-1)
    c: Diameter(g0) = 18.5
    c: PointOnObject(g0,g-2)
    c: Coincident(g1,g0)
    c: PointOnObject(g2,g-2)
    c: Coincident(g0,g2)
    c: Coincident(g0,g2)
    c: Tangent(g1,g3) = -1.5708
    c: Coincident(g3,g4)
    c: Coincident(g5,g1)
    c: Horizontal(g5)
    c: Coincident(g6,g7)
    c: Horizontal(g7)
    c: Coincident(g5,g6)
    c: Coincident(g4,g7)
    c: Coincident(g0,g2)
FEATURE [PartDesign::Pad] Pad360
  Length = 5
  Length2 = 100
  Profile = -> Sketch836
  Type = 0
FEATURE [Sketcher::SketchObject] Sketch839
  MapMode = 5
  Support = -> [XY_Plane032]
  sketch-geometry (3):
    g0: ArcOfCircle CenterX=0 CenterY=0 CenterZ=0 NormalX=0 NormalY=0 NormalZ=1 AngleXU=0 Radius=9.25 StartAngle=4.89304 EndAngle=10.8149
    g1: Circle CenterX=0 CenterY=0 CenterZ=0 NormalX=0 NormalY=0 NormalZ=1 AngleXU=0 Radius=11.3567
    g2: ArcOfCircle CenterX=0 CenterY=-8.15786 CenterZ=0 NormalX=0 NormalY=0 NormalZ=1 AngleXU=0 Radius=1.91017 StartAngle=3.65707 EndAngle=5.76771
  constraints (7):
    c: Coincident(g0,g-1)
    c: Coincident(g1,g0)
    c: Diameter(g0) = 18.5
    c: PointOnObject(g2,g-2)
    c: Coincident(g0,g2)
    c: Coincident(g0,g2)
    c: Coincident(g0,g2)
FEATURE [PartDesign::Pad] Pad362
  BaseFeature = -> Pad360
  Length = 20
  Length2 = 100
  Profile = -> Sketch839
  Type = 0
FEATURE [PartDesign::Body] Body026
  Group = -> [Sketch836,Pad360,Sketch839,Pad362]
  Origin = -> Origin032
  Placement = pos=(17.7,-32.8,9) rot=(0,0,1;0rad)
  Tip = -> Pad362
FEATURE [Mesh::Feature] main
  Placement = pos=(195,-113,0) rot=(0,0,1;0rad)
FEATURE [Sketcher::SketchObject] Sketch786
  AttachmentOffset = pos=(0,0,62) rot=(0,0,1;0rad)
  MapMode = 5
  Placement = pos=(0,0,62) rot=(0,0,1;0rad)
  Support = -> [XY_Plane063]
  sketch-geometry (24):
    g0: Circle CenterX=2.56663 CenterY=2.77975 CenterZ=0 NormalX=0 NormalY=0 NormalZ=1 AngleXU=0 Radius=9.5
    g1: LineSegment StartX=-6.48502 StartY=14.2101 StartZ=0 EndX=14.3142 EndY=11.9837 EndZ=0
    g2: LineSegment StartX=14.3142 StartY=11.9837 StartZ=0 EndX=13.827 EndY=7.08238 EndZ=0
    g3: LineSegment StartX=-7.61412 StartY=-4.42715 StartZ=0 EndX=-8.09554 EndY=-1.9332 EndZ=0
    g4: LineSegment StartX=-7.01232 StartY=9.61086 StartZ=0 EndX=-6.48502 EndY=14.2101 EndZ=0
    g5: LineSegment StartX=13.827 StartY=7.08238 StartZ=0 EndX=14.121 EndY=4.7794 EndZ=0
    g6: LineSegment StartX=14.1729 StartY=1.16342 StartZ=0 EndX=14.1118 EndY=0.543408 EndZ=0
    g7: LineSegment StartX=13.819 StartY=-0.764609 StartZ=0 EndX=12.9093 EndY=-3.31883 EndZ=0
    g8: LineSegment StartX=-7.01232 StartY=9.61086 StartZ=0 EndX=-8.31533 EndY=6.44639 EndZ=0
    g9: LineSegment StartX=-8.31533 StartY=6.44639 StartZ=0 EndX=-8.23581 EndY=-0.549404 EndZ=0
    g10: LineSegment StartX=-2.38252 StartY=-8.5621 StartZ=0 EndX=-0.561662 EndY=-8.90879 EndZ=0
    g11: LineSegment StartX=2.72265 StartY=-9.21868 StartZ=0 EndX=5.82382 EndY=-9.21868 EndZ=0
    g12: LineSegment StartX=8.69886 StartY=-8.66143 StartZ=0 EndX=9.46465 EndY=-8.35298 EndZ=0
    g13: LineSegment StartX=10.9864 StartY=-7.01277 StartZ=0 EndX=12.1226 EndY=-4.97953 EndZ=0
    g14: LineSegment StartX=12.1226 StartY=-4.97953 StartZ=0 EndX=12.9093 EndY=-3.31883 EndZ=0
    g15: LineSegment StartX=-6.88263 StartY=-5.64591 StartZ=0 EndX=-4.48253 EndY=-7.58817 EndZ=0
    g16: ArcOfCircle CenterX=-0.469524 CenterY=-0.461135 CenterZ=0 NormalX=0 NormalY=0 NormalZ=1 AngleXU=0 Radius=7.76679 StartAngle=3.15296 EndAngle=3.33228
    g17: ArcOfCircle CenterX=-5.57835 CenterY=-4.03418 CenterZ=0 NormalX=0 NormalY=0 NormalZ=1 AngleXU=0 Radius=2.07336 StartAngle=3.33228 EndAngle=4.03204
    g18: ArcOfCircle CenterX=-1.49391 CenterY=-3.89507 CenterZ=0 NormalX=0 NormalY=0 NormalZ=1 AngleXU=0 Radius=4.75087 StartAngle=4.03204 EndAngle=4.52424
    g19: ArcOfCircle CenterX=2.72265 CenterY=8.34073 CenterZ=0 NormalX=0 NormalY=0 NormalZ=1 AngleXU=0 Radius=17.5594 StartAngle=4.52424 EndAngle=4.71239
    g20: ArcOfCircle CenterX=5.82382 CenterY=-1.52341 CenterZ=0 NormalX=0 NormalY=0 NormalZ=1 AngleXU=0 Radius=7.69527 StartAngle=4.71239 EndAngle=5.09529
    g21: ArcOfCircle CenterX=8.32605 CenterY=-5.52611 CenterZ=0 NormalX=0 NormalY=0 NormalZ=1 AngleXU=0 Radius=3.04756 StartAngle=5.09529 EndAngle=5.77359
    g22: ArcOfCircle CenterX=-1.83848 CenterY=2.74201 CenterZ=0 NormalX=0 NormalY=0 NormalZ=1 AngleXU=0 Radius=16.089 StartAngle=6.18491 EndAngle=6.41016
    g23: ArcOfCircle CenterX=8.62868 CenterY=1.084 CenterZ=0 NormalX=0 NormalY=0 NormalZ=1 AngleXU=0 Radius=5.5097 StartAngle=5.94103 EndAngle=6.18491
  constraints (27):
    c: Diameter(g0) = 19
    c: DistanceX(g0) = 2.56663
    c: DistanceY(g0) = 2.77975
    c: Coincident(g1,g2)
    c: Coincident(g4,g1)
    c: Coincident(g2,g5)
    c: Coincident(g4,g8)
    c: Coincident(g8,g9)
    c: Horizontal(g11)
    c: Coincident(g13,g14)
    c: Coincident(g14,g7)
    c: Tangent(g9,g16) = -1.5708
    c: Tangent(g3,g16) = 1.5708
    c: Tangent(g3,g17) = 1.5708
    c: Tangent(g15,g17) = -1.5708
    c: Tangent(g15,g18) = -1.5708
    c: Tangent(g10,g18) = -1.5708
    c: Tangent(g10,g19) = -1.5708
    c: Tangent(g11,g19) = -1.5708
    c: Tangent(g11,g20) = -1.5708
    c: Tangent(g12,g20) = -1.5708
    c: Tangent(g12,g21) = -1.5708
    c: Tangent(g13,g21) = -1.5708
    c: Tangent(g5,g22) = 1.5708
    c: Tangent(g6,g22) = 1.5708
    c: Tangent(g6,g23) = 1.5708
    c: Tangent(g7,g23) = 1.5708
FEATURE [PartDesign::Pad] Pad342
  Length = 31
  Length2 = 100
  Profile = -> Sketch786
  Reversed = true
  Type = 0
FEATURE [Sketcher::SketchObject] Sketch800
  MapMode = 5
  Placement = pos=(0,0,0) rot=(0.57735,0.57735,0.57735;2.0944rad)
  Support = -> [YZ_Plane063]
  sketch-geometry (9):
    g0: LineSegment StartX=15.6688 StartY=56.0081 StartZ=0 EndX=7.64981 EndY=56.0081 EndZ=0
    g1: LineSegment StartX=7.64981 StartY=56.0081 StartZ=0 EndX=7.64981 EndY=41.1953 EndZ=0
    g2: LineSegment StartX=7.64981 StartY=41.1953 StartZ=0 EndX=15.6688 EndY=41.1953 EndZ=0
    g3: LineSegment StartX=15.6688 StartY=41.1953 StartZ=0 EndX=15.6688 EndY=56.0081 EndZ=0
    g4: Circle CenterX=2.54395 CenterY=46.081 CenterZ=0 NormalX=0 NormalY=0 NormalZ=1 AngleXU=0 Radius=3.64009
    g5: LineSegment StartX=7.64981 StartY=34.7868 StartZ=0 EndX=15.6688 EndY=34.7868 EndZ=0
    g6: LineSegment StartX=15.6688 StartY=34.7868 StartZ=0 EndX=15.6688 EndY=29.8776 EndZ=0
    g7: LineSegment StartX=15.6688 StartY=29.8776 StartZ=0 EndX=7.64981 EndY=29.8776 EndZ=0
    g8: LineSegment StartX=7.64981 StartY=29.8776 StartZ=0 EndX=7.64981 EndY=34.7868 EndZ=0
  constraints (18):
    c: Coincident(g0,g1)
    c: Coincident(g1,g2)
    c: Coincident(g2,g3)
    c: Coincident(g3,g0)
    c: Horizontal(g0)
    c: Horizontal(g2)
    c: Vertical(g1)
    c: Vertical(g3)
    c: Coincident(g5,g6)
    c: Coincident(g6,g7)
    c: Coincident(g7,g8)
    c: Coincident(g8,g5)
    c: Horizontal(g5)
    c: Horizontal(g7)
    c: Vertical(g6)
    c: Vertical(g8)
    c: PointOnObject(g5,g1)
    c: PointOnObject(g5,g3)
FEATURE [PartDesign::Pocket] Pocket216
  BaseFeature = -> Pad342
  Length = 5
  Length2 = 100
  Midplane = true
  Profile = -> Sketch800
  Type = 1
FEATURE [Sketcher::SketchObject] Sketch801
  MapMode = 5
  Placement = pos=(0,0,0) rot=(1,0,0;1.5708rad)
  Support = -> [XZ_Plane063]
  sketch-geometry (18):
    g0: LineSegment [constr] StartX=9.37786 StartY=65.0161 StartZ=0 EndX=9.37786 EndY=23.6565 EndZ=0
    g1: LineSegment [constr] StartX=-3.5134 StartY=64.9109 StartZ=0 EndX=-3.5134 EndY=23.867 EndZ=0
    g2: LineSegment StartX=-3.5134 StartY=63.3329 StartZ=0 EndX=9.37786 EndY=63.3329 EndZ=0
    g3: LineSegment StartX=9.37786 StartY=63.3329 StartZ=0 EndX=9.37786 EndY=60.9213 EndZ=0
    g4: LineSegment StartX=9.37786 StartY=60.9213 StartZ=0 EndX=-3.5134 EndY=60.9213 EndZ=0
    g5: LineSegment StartX=-3.5134 StartY=60.9213 StartZ=0 EndX=-3.5134 EndY=63.3329 EndZ=0
    g6: LineSegment StartX=-3.5134 StartY=31.7622 StartZ=0 EndX=9.37786 EndY=31.7622 EndZ=0
    g7: LineSegment StartX=9.37786 StartY=31.7622 StartZ=0 EndX=9.37786 EndY=30.1071 EndZ=0
    g8: LineSegment StartX=9.37786 StartY=30.1071 StartZ=0 EndX=-3.5134 EndY=30.1071 EndZ=0
    g9: LineSegment StartX=-3.5134 StartY=30.1071 StartZ=0 EndX=-3.5134 EndY=31.7622 EndZ=0
    g10: LineSegment StartX=-3.5134 StartY=37.6848 StartZ=0 EndX=9.37786 EndY=37.6848 EndZ=0
    g11: LineSegment StartX=9.37786 StartY=37.6848 StartZ=0 EndX=9.37786 EndY=35.1785 EndZ=0
    g12: LineSegment StartX=9.37786 StartY=35.1785 StartZ=0 EndX=-3.5134 EndY=35.1785 EndZ=0
    g13: LineSegment StartX=-3.5134 StartY=35.1785 StartZ=0 EndX=-3.5134 EndY=37.6848 EndZ=0
    g14: LineSegment StartX=-3.5134 StartY=54.8755 StartZ=0 EndX=9.37786 EndY=54.8755 EndZ=0
    g15: LineSegment StartX=9.37786 StartY=54.8755 StartZ=0 EndX=9.37786 EndY=52.5111 EndZ=0
    g16: LineSegment StartX=9.37786 StartY=52.5111 StartZ=0 EndX=-3.5134 EndY=52.5111 EndZ=0
    g17: LineSegment StartX=-3.5134 StartY=52.5111 StartZ=0 EndX=-3.5134 EndY=54.8755 EndZ=0
  constraints (42):
    c: Vertical(g0)
    c: Vertical(g1)
    c: Coincident(g2,g3)
    c: Coincident(g3,g4)
    c: Coincident(g4,g5)
    c: Coincident(g5,g2)
    c: Horizontal(g2)
    c: Horizontal(g4)
    c: Vertical(g3)
    c: Vertical(g5)
    c: PointOnObject(g2,g1)
    c: PointOnObject(g3,g0)
    c: Coincident(g6,g7)
    c: Coincident(g7,g8)
    c: Coincident(g8,g9)
    c: Coincident(g9,g6)
    c: Horizontal(g6)
    c: Horizontal(g8)
    c: Vertical(g7)
    c: Vertical(g9)
    c: PointOnObject(g6,g1)
    c: PointOnObject(g7,g0)
    c: Coincident(g10,g11)
    c: Coincident(g11,g12)
    c: Coincident(g12,g13)
    c: Coincident(g13,g10)
    c: Horizontal(g10)
    c: Horizontal(g12)
    c: Vertical(g11)
    c: Vertical(g13)
    c: PointOnObject(g10,g1)
    c: PointOnObject(g11,g0)
    c: Coincident(g14,g15)
    c: Coincident(g15,g16)
    c: Coincident(g16,g17)
    c: Coincident(g17,g14)
    c: Horizontal(g14)
    c: Horizontal(g16)
    c: Vertical(g15)
    c: Vertical(g17)
    c: PointOnObject(g14,g1)
    c: PointOnObject(g15,g0)
FEATURE [PartDesign::Pocket] Pocket217
  BaseFeature = -> Pocket216
  Length = 5
  Length2 = 100
  Profile = -> Sketch801
  Type = 1
FEATURE [PartDesign::Body] Body063  label="newmain-proxholder"
  Group = -> [Sketch786,Pad342,Sketch800,Pocket216,Sketch801,Pocket217]
  Origin = -> Origin063
  Placement = pos=(1.04528,-9.94522,-20.5) rot=(0,0,1;0.10472rad)
  Tip = -> Pocket217
FEATURE [Sketcher::SketchObject] Sketch840
  AttachmentOffset = pos=(0,0,35) rot=(0,0,1;0rad)
  MapMode = 5
  Placement = pos=(35,-7.8e-15,7.8e-15) rot=(0.57735,0.57735,0.57735;2.0944rad)
  Support = -> [YZ_Plane]
  sketch-geometry (8):
    g0: LineSegment StartX=-43.608 StartY=90.4499 StartZ=0 EndX=-38.6963 EndY=90.4499 EndZ=0
    g1: LineSegment StartX=-38.6963 StartY=90.4499 StartZ=0 EndX=-2.34978 EndY=53.4895 EndZ=0
    g2: LineSegment StartX=-2.34978 StartY=53.4895 StartZ=0 EndX=-2.10419 EndY=47.3498 EndZ=0
    g3: LineSegment StartX=-2.10419 StartY=47.3498 StartZ=0 EndX=-43.608 EndY=90.4499 EndZ=0
    g4: LineSegment StartX=-36.263 StartY=17.7061 StartZ=0 EndX=-30.3393 EndY=17.7061 EndZ=0
    g5: LineSegment StartX=-30.3393 StartY=17.7061 StartZ=0 EndX=-1.60594 EndY=38.713 EndZ=0
    g6: LineSegment StartX=-1.60594 StartY=38.713 StartZ=0 EndX=-2.09711 EndY=43.1336 EndZ=0
    g7: LineSegment StartX=-2.09711 StartY=43.1336 StartZ=0 EndX=-36.263 EndY=17.7061 EndZ=0
  constraints (10):
    c: Horizontal(g0)
    c: Coincident(g0,g1)
    c: Coincident(g1,g2)
    c: Coincident(g2,g3)
    c: Coincident(g3,g0)
    c: Horizontal(g4)
    c: Coincident(g4,g5)
    c: Coincident(g5,g6)
    c: Coincident(g6,g7)
    c: Coincident(g7,g4)
FEATURE [PartDesign::Pad] Pad363
  BaseFeature = -> Pad355
  Length = 6
  Length2 = 100
  Placement = pos=(0,0,0) rot=(1,0,0;1.5708rad)
  Profile = -> Sketch840
  Type = 0
FEATURE [PartDesign::Body] Body
  Group = -> [Sketch,Pad,Sketch812,Pad348,Sketch813,Pad349,Sketch821,Pad355,Sketch840,Pad363]
  Origin = -> Origin
  Tip = -> Pad363
FEATURE [Sketcher::SketchObject] Sketch841
  MapMode = 5
  Support = -> [XY_Plane064]
  sketch-geometry (4):
    g0: ArcOfCircle CenterX=0 CenterY=0 CenterZ=0 NormalX=0 NormalY=0 NormalZ=1 AngleXU=0 Radius=2.6 StartAngle=2.33252 EndAngle=7.09226
    g1: LineSegment StartX=-1.79444 StartY=1.88149 StartZ=0 EndX=1.79444 EndY=1.88149 EndZ=0
    g2: GeomPoint X=0 Y=-2.6 Z=0
    g3: Circle CenterX=0 CenterY=0 CenterZ=0 NormalX=0 NormalY=0 NormalZ=1 AngleXU=0 Radius=5.57502
  constraints (8):
    c: Coincident(g0,g-1)
    c: Diameter(g0) = 5.2
    c: Horizontal(g1)
    c: PointOnObject(g2,g-2)
    c: PointOnObject(g2,g0)
    c: Coincident(g0,g1)
    c: Coincident(g0,g1)
    c: Coincident(g3,g0)
FEATURE [PartDesign::Pad] Pad364
  Length = 20
  Length2 = 100
  Profile = -> Sketch841
  Type = 0
FEATURE [Sketcher::SketchObject] Sketch842
  MapMode = 5
  Support = -> [XY_Plane064]
  sketch-geometry (1):
    g0: Circle CenterX=0 CenterY=0 CenterZ=0 NormalX=0 NormalY=0 NormalZ=1 AngleXU=0 Radius=5.56031
FEATURE [PartDesign::Pad] Pad365
  BaseFeature = -> Pad364
  Length = 18
  Length2 = 100
  Profile = -> Sketch842
  Reversed = true
  Type = 0
FEATURE [Sketcher::SketchObject] Sketch843
  AttachmentOffset = pos=(-9,0,9) rot=(0,-1,0;0.785398rad)
  MapMode = 5
  Placement = pos=(-9,0,9) rot=(0,-1,0;0.785398rad)
  Support = -> [XY_Plane064]
  sketch-geometry (1):
    g0: Circle CenterX=-8.74225 CenterY=0 CenterZ=0 NormalX=0 NormalY=0 NormalZ=1 AngleXU=0 Radius=5.57928
FEATURE [PartDesign::Pad] Pad366
  BaseFeature = -> Pad365
  Length = 20
  Length2 = 100
  Profile = -> Sketch843
  Reversed = true
  Type = 0
FEATURE [Sketcher::SketchObject] Sketch844
  AttachmentOffset = pos=(-9,0,9) rot=(0,-1,0;0.785398rad)
  MapMode = 5
  Placement = pos=(-9,0,9) rot=(0,-1,0;0.785398rad)
  Support = -> [XY_Plane064]
  sketch-geometry (1):
    g0: Circle CenterX=-8.74225 CenterY=0 CenterZ=0 NormalX=0 NormalY=0 NormalZ=1 AngleXU=0 Radius=2.85
  constraints (1):
    c: Diameter(g0) = 5.7
FEATURE [PartDesign::Pocket] Pocket224
  BaseFeature = -> Pad366
  Length = 20
  Length2 = 100
  Profile = -> Sketch844
  Type = 0
FEATURE [Sketcher::SketchObject] Sketch845
  MapMode = 5
  Support = -> [XY_Plane064]
  sketch-geometry (1):
    g0: Circle CenterX=0 CenterY=0 CenterZ=0 NormalX=0 NormalY=0 NormalZ=1 AngleXU=0 Radius=2.95
  constraints (1):
    c: Diameter(g0) = 5.9
FEATURE [PartDesign::Pocket] Pocket225
  BaseFeature = -> Pocket224
  Length = 5
  Length2 = 100
  Profile = -> Sketch845
  Type = 1
FEATURE [PartDesign::Body] Body064
  Group = -> [Sketch841,Pad364,Sketch842,Pad365,Sketch843,Pad366,Sketch844,Pocket224,Sketch845,Pocket225]
  Origin = -> Origin064
  Placement = pos=(-52,-108,0) rot=(0,0,1;0rad)
  Tip = -> Pocket225
